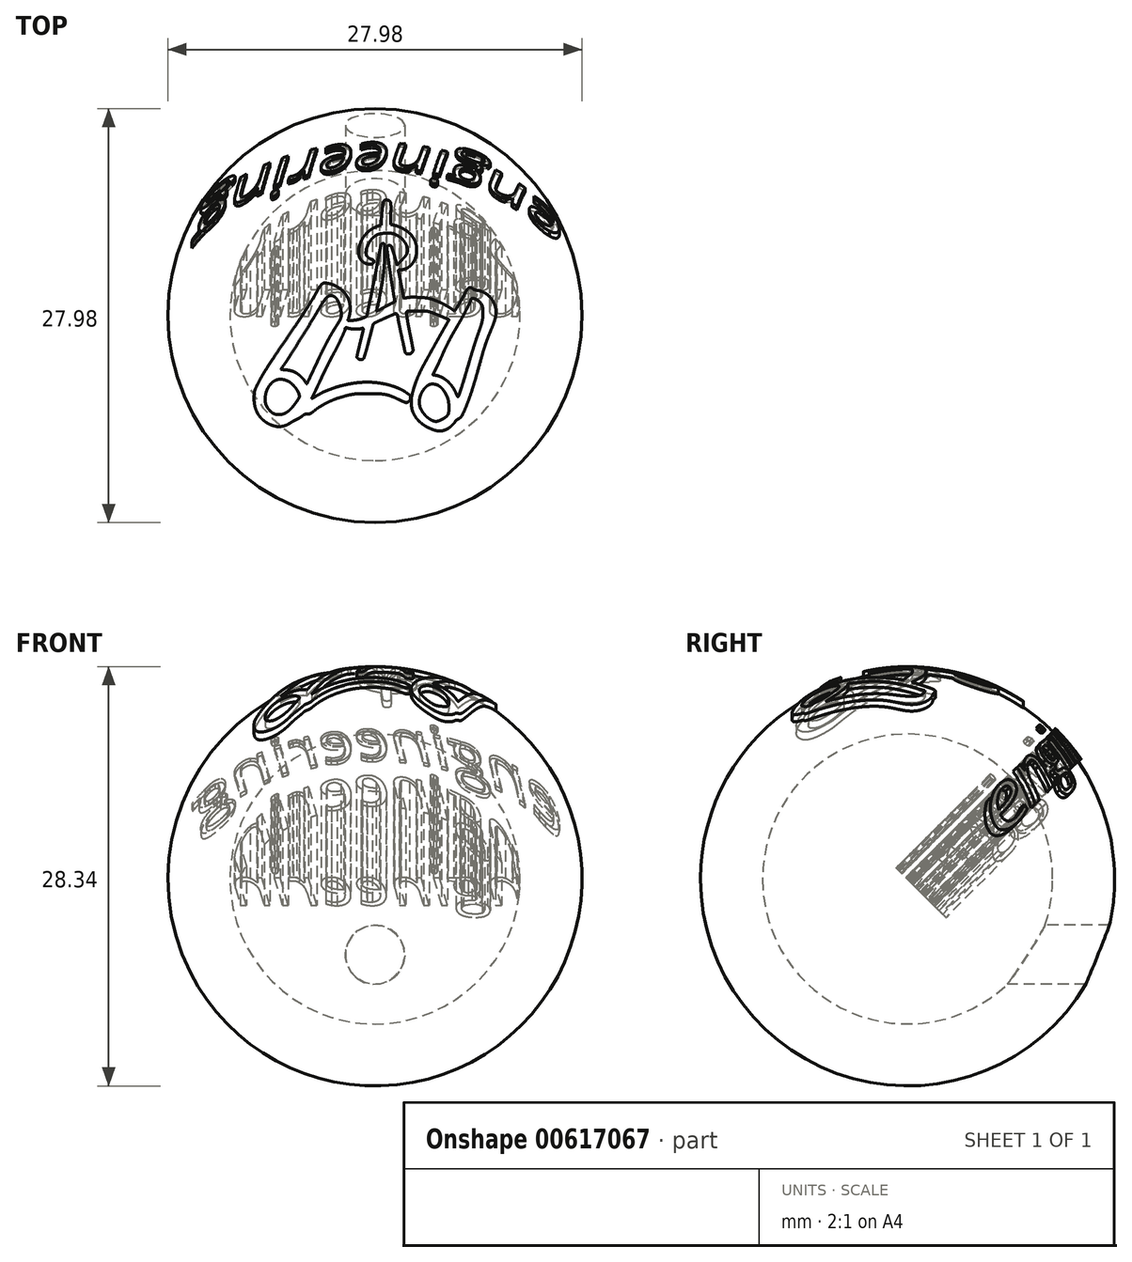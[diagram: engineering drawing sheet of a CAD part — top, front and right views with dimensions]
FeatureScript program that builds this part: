
annotation { "Feature Type Name" : "Feature", "Feature Type Description" : "" }
export const myFeature = defineFeature(function(context is Context, id is Id, definition is map)
    precondition{}
    {
        {
            var Q0;
            Q0=qCreatedBy(makeId("Top.planeOp"),FACE);
            var sketch = newSketch(context, id + "F0", { "sketchPlane" : qUnion([Q0])});
            skLineSegment(sketch, "E0", {"start": v(0, -10) * mm, "end": v(0, 10) * mm});
            skArc(sketch, "E1", {"start": v(0, 10) * mm, "mid": v(-10, 0) * mm, "end": v(0, -10) * mm});
            skSolve(sketch);
        }
        {
            var Q0;
            {var subQ0=sQuery(id+"F0.wireOp",EDGE,"E1");Q0=makeQuery(id+"F0.imprint","IMPRINT",FACE,{"disambiguationData":[TD([[makeQuery(id+"F0.imprint","IMPRINT",EDGE,{"derivedFrom":subQ0}),1.0]])]});}
            var Q1;
            Q1=sQuery(id+"F0.wireOp",EDGE,"E0");
            revolve(context, id + "F1", {"entities" : qUnion([Q0]), "axis" : qUnion([Q1]), "revolveType" : RevolveType.FULL});
        }
        {
            var Q0;
            Q0=makeQuery(id+"F1.opRevolve","SWEPT_BODY",BODY,{"disambiguationData":[OSD([sQuery(id+"F0.wireOp",EDGE,"E0"),sQuery(id+"F0.wireOp",EDGE,"E1")])]});
            var Q1;
            Q1=sQuery(id+"F0.wireOp",VERTEX,"NPe4G0ez-t7S9-9isL-QO5v-uuJu600mHcIT.center");
            var Q2;
            Q2=sQuery(id+"F0.wireOp",VERTEX,"E1.center");
            transform(context, id + "F2", {"entities" : qUnion([Q0]), "transformType" : TransformType.SCALE_UNIFORMLY, "scale" : 33.3, "scalePoint" : qUnion([Q2]), "makeCopy" : false});
        }
        {
            var Q0;
            Q0=qCreatedBy(makeId("Top.planeOp"),FACE);
            var sketch = newSketch(context, id + "F3", { "sketchPlane" : qUnion([Q0])});
            skArc(sketch, "E2", {"start": v(14.34, 184.46) * mm, "mid": v(13.65, 183.38) * mm, "end": v(13.25, 182.16) * mm});
            skArc(sketch, "E3", {"start": v(13.25, 182.16) * mm, "mid": v(12.71, 179.17) * mm, "end": v(12.25, 176.16) * mm});
            skArc(sketch, "E4", {"start": v(12.25, 176.16) * mm, "mid": v(11.73, 172.13) * mm, "end": v(11.32, 168.08) * mm});
            skArc(sketch, "E5", {"start": v(11.32, 168.08) * mm, "mid": v(10.9, 162.81) * mm, "end": v(10.53, 157.54) * mm});
            skLineSegment(sketch, "E6", {"start": v(10.53, 157.54) * mm, "end": v(9.8, 145.67) * mm});
            skLineSegment(sketch, "E7", {"start": v(9.8, 145.67) * mm, "end": v(3.78, 143.5) * mm});
            skArc(sketch, "E8", {"start": v(3.78, 143.5) * mm, "mid": v(-1.65, 141.13) * mm, "end": v(-6.72, 138.07) * mm});
            skArc(sketch, "E9", {"start": v(-6.72, 138.07) * mm, "mid": v(-11.38, 134.36) * mm, "end": v(-15.52, 130.08) * mm});
            skArc(sketch, "E10", {"start": v(-15.52, 130.08) * mm, "mid": v(-19.1, 125.3) * mm, "end": v(-22.03, 120.08) * mm});
            skArc(sketch, "E11", {"start": v(-22.03, 120.08) * mm, "mid": v(-24.3, 114.52) * mm, "end": v(-25.83, 108.72) * mm});
            skArc(sketch, "E12", {"start": v(-25.83, 108.72) * mm, "mid": v(-26.4, 104.16) * mm, "end": v(-26.28, 99.57) * mm});
            skArc(sketch, "E13", {"start": v(-26.28, 99.57) * mm, "mid": v(-25.48, 95.49) * mm, "end": v(-23.89, 91.65) * mm});
            skArc(sketch, "E14", {"start": v(-23.89, 91.65) * mm, "mid": v(-21.73, 88.51) * mm, "end": v(-18.93, 85.93) * mm});
            skArc(sketch, "E15", {"start": v(-18.93, 85.93) * mm, "mid": v(-15.67, 84.07) * mm, "end": v(-12.07, 83) * mm});
            skArc(sketch, "E16", {"start": v(-12.07, 83) * mm, "mid": v(-9.95, 82.7) * mm, "end": v(-7.82, 82.55) * mm});
            skArc(sketch, "E17", {"start": v(-7.82, 82.55) * mm, "mid": v(-6.26, 82.62) * mm, "end": v(-4.73, 82.96) * mm});
            skArc(sketch, "E18", {"start": v(-4.73, 82.96) * mm, "mid": v(-3.68, 83.44) * mm, "end": v(-2.8, 84.19) * mm});
            skArc(sketch, "E19", {"start": v(-2.8, 84.19) * mm, "mid": v(-2.19, 85.1) * mm, "end": v(-1.9, 86.15) * mm});
            skArc(sketch, "E20", {"start": v(-1.9, 86.15) * mm, "mid": v(-1.84, 86.88) * mm, "end": v(-1.86, 87.6) * mm});
            skArc(sketch, "E21", {"start": v(-1.86, 87.6) * mm, "mid": v(-1.96, 88.1) * mm, "end": v(-2.19, 88.56) * mm});
            skArc(sketch, "E22", {"start": v(-2.19, 88.56) * mm, "mid": v(-2.53, 88.96) * mm, "end": v(-2.96, 89.27) * mm});
            skArc(sketch, "E23", {"start": v(-2.96, 89.27) * mm, "mid": v(-3.66, 89.62) * mm, "end": v(-4.4, 89.92) * mm});
            skArc(sketch, "E24", {"start": v(-4.4, 89.92) * mm, "mid": v(-7.1, 91.04) * mm, "end": v(-9.71, 92.4) * mm});
            skArc(sketch, "E25", {"start": v(-9.71, 92.4) * mm, "mid": v(-11.45, 93.66) * mm, "end": v(-12.88, 95.27) * mm});
            skArc(sketch, "E26", {"start": v(-12.88, 95.27) * mm, "mid": v(-13.84, 97.04) * mm, "end": v(-14.34, 98.99) * mm});
            skArc(sketch, "E27", {"start": v(-14.34, 98.99) * mm, "mid": v(-14.52, 101.49) * mm, "end": v(-14.38, 104) * mm});
            skArc(sketch, "E28", {"start": v(-14.38, 104) * mm, "mid": v(-13.95, 106.46) * mm, "end": v(-13.24, 108.87) * mm});
            skArc(sketch, "E29", {"start": v(-13.24, 108.87) * mm, "mid": v(-12.08, 111.8) * mm, "end": v(-10.77, 114.65) * mm});
            skArc(sketch, "E30", {"start": v(-10.77, 114.65) * mm, "mid": v(-9.27, 117.46) * mm, "end": v(-7.61, 120.17) * mm});
            skArc(sketch, "E31", {"start": v(-7.61, 120.17) * mm, "mid": v(-6.07, 122.28) * mm, "end": v(-4.32, 124.22) * mm});
            skArc(sketch, "E32", {"start": v(-4.32, 124.22) * mm, "mid": v(-2.04, 126.3) * mm, "end": v(0.42, 128.16) * mm});
            skArc(sketch, "E33", {"start": v(0.42, 128.16) * mm, "mid": v(2.78, 129.56) * mm, "end": v(5.3, 130.64) * mm});
            skArc(sketch, "E34", {"start": v(5.3, 130.64) * mm, "mid": v(8.18, 131.48) * mm, "end": v(11.13, 131.98) * mm});
            skArc(sketch, "E35", {"start": v(11.13, 131.98) * mm, "mid": v(14.95, 132.3) * mm, "end": v(18.8, 132.4) * mm});
            skArc(sketch, "E36", {"start": v(18.8, 132.4) * mm, "mid": v(21.68, 132.38) * mm, "end": v(24.57, 132.3) * mm});
            skArc(sketch, "E37", {"start": v(24.57, 132.3) * mm, "mid": v(26.3, 132.18) * mm, "end": v(28.03, 131.95) * mm});
            skArc(sketch, "E38", {"start": v(28.03, 131.95) * mm, "mid": v(29.48, 131.62) * mm, "end": v(30.9, 131.17) * mm});
            skArc(sketch, "E39", {"start": v(30.9, 131.17) * mm, "mid": v(32.61, 130.47) * mm, "end": v(34.3, 129.7) * mm});
            skArc(sketch, "E40", {"start": v(34.3, 129.7) * mm, "mid": v(38, 127.6) * mm, "end": v(41.43, 125.08) * mm});
            skArc(sketch, "E41", {"start": v(41.43, 125.08) * mm, "mid": v(44.5, 122.2) * mm, "end": v(47.2, 118.99) * mm});
            skArc(sketch, "E42", {"start": v(47.2, 118.99) * mm, "mid": v(49.33, 115.7) * mm, "end": v(51, 112.16) * mm});
            skArc(sketch, "E43", {"start": v(51, 112.16) * mm, "mid": v(51.96, 108.85) * mm, "end": v(52.28, 105.42) * mm});
            skArc(sketch, "E44", {"start": v(52.28, 105.42) * mm, "mid": v(52.18, 103.4) * mm, "end": v(51.87, 101.4) * mm});
            skArc(sketch, "E45", {"start": v(51.87, 101.4) * mm, "mid": v(51.38, 99.73) * mm, "end": v(50.63, 98.17) * mm});
            skArc(sketch, "E46", {"start": v(50.63, 98.17) * mm, "mid": v(49.39, 96.27) * mm, "end": v(47.97, 94.5) * mm});
            skArc(sketch, "E47", {"start": v(47.97, 94.5) * mm, "mid": v(45.12, 91.31) * mm, "end": v(42.2, 88.18) * mm});
            skLineSegment(sketch, "E48", {"start": v(42.2, 88.18) * mm, "end": v(35.62, 81.22) * mm});
            skLineSegment(sketch, "E49", {"start": v(35.62, 81.22) * mm, "end": v(31.41, 95.8) * mm});
            skArc(sketch, "E50", {"start": v(31.41, 95.8) * mm, "mid": v(30.57, 98.66) * mm, "end": v(29.7, 101.5) * mm});
            skArc(sketch, "E51", {"start": v(29.7, 101.5) * mm, "mid": v(28.9, 104.02) * mm, "end": v(28.04, 106.52) * mm});
            skArc(sketch, "E52", {"start": v(28.04, 106.52) * mm, "mid": v(27.3, 108.6) * mm, "end": v(26.54, 110.68) * mm});
            skArc(sketch, "E53", {"start": v(26.54, 110.68) * mm, "mid": v(26.24, 111.27) * mm, "end": v(25.83, 111.78) * mm});
            skArc(sketch, "E54", {"start": v(25.83, 111.78) * mm, "mid": v(25.48, 112.08) * mm, "end": v(25.08, 112.32) * mm});
            skArc(sketch, "E55", {"start": v(25.08, 112.32) * mm, "mid": v(24.62, 112.5) * mm, "end": v(24.14, 112.63) * mm});
            skArc(sketch, "E56", {"start": v(24.14, 112.63) * mm, "mid": v(23.6, 112.7) * mm, "end": v(23.05, 112.7) * mm});
            skArc(sketch, "E57", {"start": v(23.05, 112.7) * mm, "mid": v(22.46, 112.63) * mm, "end": v(21.88, 112.51) * mm});
            skArc(sketch, "E58", {"start": v(21.88, 112.51) * mm, "mid": v(21.22, 112.3) * mm, "end": v(20.59, 112.04) * mm});
            skArc(sketch, "E59", {"start": v(20.59, 112.04) * mm, "mid": v(20.16, 111.77) * mm, "end": v(19.82, 111.4) * mm});
            skArc(sketch, "E60", {"start": v(19.82, 111.4) * mm, "mid": v(19.56, 110.94) * mm, "end": v(19.41, 110.43) * mm});
            skArc(sketch, "E61", {"start": v(19.41, 110.43) * mm, "mid": v(19.32, 109.68) * mm, "end": v(19.3, 108.93) * mm});
            skArc(sketch, "E62", {"start": v(19.3, 108.93) * mm, "mid": v(19.39, 106.06) * mm, "end": v(19.67, 103.2) * mm});
            skArc(sketch, "E63", {"start": v(19.67, 103.2) * mm, "mid": v(20.92, 93.82) * mm, "end": v(22.2, 84.45) * mm});
            skArc(sketch, "E64", {"start": v(22.2, 84.45) * mm, "mid": v(23.65, 74.23) * mm, "end": v(25.16, 64.02) * mm});
            skArc(sketch, "E65", {"start": v(25.16, 64.02) * mm, "mid": v(26.64, 54.39) * mm, "end": v(28.18, 44.76) * mm});
            skLineSegment(sketch, "E66", {"start": v(28.18, 44.76) * mm, "end": v(31.9, 22.13) * mm});
            skLineSegment(sketch, "E67", {"start": v(31.9, 22.13) * mm, "end": v(26.35, 19.42) * mm});
            skArc(sketch, "E68", {"start": v(26.35, 19.42) * mm, "mid": v(24.97, 18.74) * mm, "end": v(23.6, 18.04) * mm});
            skArc(sketch, "E69", {"start": v(23.6, 18.04) * mm, "mid": v(21.71, 17.05) * mm, "end": v(19.82, 16.05) * mm});
            skArc(sketch, "E70", {"start": v(19.82, 16.05) * mm, "mid": v(17.78, 14.95) * mm, "end": v(15.74, 13.84) * mm});
            skArc(sketch, "E71", {"start": v(15.74, 13.84) * mm, "mid": v(13.84, 12.8) * mm, "end": v(11.94, 11.74) * mm});
            skArc(sketch, "E72", {"start": v(11.94, 11.74) * mm, "mid": v(10.24, 10.8) * mm, "end": v(8.52, 9.86) * mm});
            skArc(sketch, "E73", {"start": v(8.52, 9.86) * mm, "mid": v(7.06, 9.08) * mm, "end": v(5.59, 8.33) * mm});
            skArc(sketch, "E74", {"start": v(5.59, 8.33) * mm, "mid": v(4.32, 7.7) * mm, "end": v(3.04, 7.07) * mm});
            skArc(sketch, "E75", {"start": v(3.04, 7.07) * mm, "mid": v(2.88, 7.04) * mm, "end": v(2.74, 7.12) * mm});
            skArc(sketch, "E76", {"start": v(2.74, 7.12) * mm, "mid": v(2.65, 7.27) * mm, "end": v(2.64, 7.44) * mm});
            skArc(sketch, "E77", {"start": v(2.64, 7.44) * mm, "mid": v(2.93, 9.01) * mm, "end": v(3.22, 10.58) * mm});
            skArc(sketch, "E78", {"start": v(3.22, 10.58) * mm, "mid": v(3.57, 12.38) * mm, "end": v(3.94, 14.18) * mm});
            skArc(sketch, "E79", {"start": v(3.94, 14.18) * mm, "mid": v(4.4, 16.3) * mm, "end": v(4.86, 18.4) * mm});
            skArc(sketch, "E80", {"start": v(4.86, 18.4) * mm, "mid": v(7.3, 29.7) * mm, "end": v(9.54, 41.06) * mm});
            skArc(sketch, "E81", {"start": v(9.54, 41.06) * mm, "mid": v(11.33, 51.39) * mm, "end": v(12.86, 61.75) * mm});
            skArc(sketch, "E82", {"start": v(12.86, 61.75) * mm, "mid": v(14.01, 71.25) * mm, "end": v(14.9, 80.77) * mm});
            skArc(sketch, "E83", {"start": v(14.9, 80.77) * mm, "mid": v(15.43, 89.58) * mm, "end": v(15.66, 98.4) * mm});
            skArc(sketch, "E84", {"start": v(15.66, 98.4) * mm, "mid": v(15.69, 103.78) * mm, "end": v(15.7, 109.17) * mm});
            skArc(sketch, "E85", {"start": v(15.7, 109.17) * mm, "mid": v(15.65, 111.11) * mm, "end": v(15.5, 113.05) * mm});
            skArc(sketch, "E86", {"start": v(15.5, 113.05) * mm, "mid": v(15.3, 114) * mm, "end": v(14.92, 114.88) * mm});
            skArc(sketch, "E87", {"start": v(14.92, 114.88) * mm, "mid": v(14.45, 115.4) * mm, "end": v(13.8, 115.66) * mm});
            skArc(sketch, "E88", {"start": v(13.8, 115.66) * mm, "mid": v(13.36, 115.7) * mm, "end": v(12.93, 115.7) * mm});
            skArc(sketch, "E89", {"start": v(12.93, 115.7) * mm, "mid": v(12.47, 115.66) * mm, "end": v(12.01, 115.6) * mm});
            skArc(sketch, "E90", {"start": v(12.01, 115.6) * mm, "mid": v(11.59, 115.51) * mm, "end": v(11.17, 115.4) * mm});
            skArc(sketch, "E91", {"start": v(11.17, 115.4) * mm, "mid": v(10.85, 115.27) * mm, "end": v(10.55, 115.1) * mm});
            skArc(sketch, "E92", {"start": v(10.55, 115.1) * mm, "mid": v(10.18, 114.74) * mm, "end": v(9.96, 114.27) * mm});
            skArc(sketch, "E93", {"start": v(9.96, 114.27) * mm, "mid": v(9.3, 111.54) * mm, "end": v(8.66, 108.8) * mm});
            skArc(sketch, "E94", {"start": v(8.66, 108.8) * mm, "mid": v(7.93, 105.55) * mm, "end": v(7.26, 102.3) * mm});
            skArc(sketch, "E95", {"start": v(7.26, 102.3) * mm, "mid": v(6.52, 98.49) * mm, "end": v(5.83, 94.68) * mm});
            skArc(sketch, "E96", {"start": v(5.83, 94.68) * mm, "mid": v(3.24, 80.45) * mm, "end": v(0.53, 66.24) * mm});
            skArc(sketch, "E97", {"start": v(0.53, 66.24) * mm, "mid": v(-2.7, 49.95) * mm, "end": v(-6.01, 33.68) * mm});
            skArc(sketch, "E98", {"start": v(-6.01, 33.68) * mm, "mid": v(-9.46, 17.03) * mm, "end": v(-12.92, 0.37) * mm});
            skArc(sketch, "E99", {"start": v(-12.92, 0.37) * mm, "mid": v(-13.36, -0.82) * mm, "end": v(-14.12, -1.85) * mm});
            skArc(sketch, "E100", {"start": v(-14.12, -1.85) * mm, "mid": v(-14.3, -2) * mm, "end": v(-14.5, -2.1) * mm});
            skArc(sketch, "E101", {"start": v(-14.5, -2.1) * mm, "mid": v(-15.47, -2.5) * mm, "end": v(-16.44, -2.9) * mm});
            skArc(sketch, "E102", {"start": v(-16.44, -2.9) * mm, "mid": v(-17.6, -3.36) * mm, "end": v(-18.75, -3.8) * mm});
            skArc(sketch, "E103", {"start": v(-18.75, -3.8) * mm, "mid": v(-20.07, -4.3) * mm, "end": v(-21.4, -4.8) * mm});
            skArc(sketch, "E104", {"start": v(-21.4, -4.8) * mm, "mid": v(-24.7, -5.86) * mm, "end": v(-28.07, -6.69) * mm});
            skArc(sketch, "E105", {"start": v(-28.07, -6.69) * mm, "mid": v(-31.93, -7.38) * mm, "end": v(-35.82, -7.87) * mm});
            skArc(sketch, "E106", {"start": v(-35.82, -7.87) * mm, "mid": v(-39.17, -8.14) * mm, "end": v(-42.54, -8.26) * mm});
            skArc(sketch, "E107", {"start": v(-42.54, -8.26) * mm, "mid": v(-43.31, -7.86) * mm, "end": v(-43.4, -7) * mm});
            skArc(sketch, "E108", {"start": v(-43.4, -7) * mm, "mid": v(-41.81, -2.55) * mm, "end": v(-40.64, 2.04) * mm});
            skArc(sketch, "E109", {"start": v(-40.64, 2.04) * mm, "mid": v(-39.95, 6.54) * mm, "end": v(-39.73, 11.1) * mm});
            skArc(sketch, "E110", {"start": v(-39.73, 11.1) * mm, "mid": v(-39.97, 15.5) * mm, "end": v(-40.7, 19.84) * mm});
            skArc(sketch, "E111", {"start": v(-40.7, 19.84) * mm, "mid": v(-41.86, 23.99) * mm, "end": v(-43.5, 27.97) * mm});
            skArc(sketch, "E112", {"start": v(-43.5, 27.97) * mm, "mid": v(-45.84, 32.18) * mm, "end": v(-48.67, 36.07) * mm});
            skArc(sketch, "E113", {"start": v(-48.67, 36.07) * mm, "mid": v(-52.02, 39.68) * mm, "end": v(-55.77, 42.88) * mm});
            skArc(sketch, "E114", {"start": v(-55.77, 42.88) * mm, "mid": v(-59.97, 45.73) * mm, "end": v(-64.46, 48.1) * mm});
            skArc(sketch, "E115", {"start": v(-64.46, 48.1) * mm, "mid": v(-69.32, 50.03) * mm, "end": v(-74.35, 51.47) * mm});
            skArc(sketch, "E116", {"start": v(-74.35, 51.47) * mm, "mid": v(-77.6, 52.06) * mm, "end": v(-80.88, 52.34) * mm});
            skArc(sketch, "E117", {"start": v(-80.88, 52.34) * mm, "mid": v(-82.95, 52.05) * mm, "end": v(-84.8, 51.08) * mm});
            skArc(sketch, "E118", {"start": v(-84.8, 51.08) * mm, "mid": v(-86.77, 49.23) * mm, "end": v(-88.38, 47.06) * mm});
            skArc(sketch, "E119", {"start": v(-88.38, 47.06) * mm, "mid": v(-91.9, 41.16) * mm, "end": v(-95.34, 35.2) * mm});
            skArc(sketch, "E120", {"start": v(-95.34, 35.2) * mm, "mid": v(-99.5, 28.01) * mm, "end": v(-103.77, 20.9) * mm});
            skArc(sketch, "E121", {"start": v(-103.77, 20.9) * mm, "mid": v(-108.75, 12.9) * mm, "end": v(-113.83, 4.98) * mm});
            skArc(sketch, "E122", {"start": v(-113.83, 4.98) * mm, "mid": v(-120.33, -4.92) * mm, "end": v(-126.92, -14.75) * mm});
            skArc(sketch, "E123", {"start": v(-126.92, -14.75) * mm, "mid": v(-135.97, -28.08) * mm, "end": v(-145.08, -41.37) * mm});
            skArc(sketch, "E124", {"start": v(-145.08, -41.37) * mm, "mid": v(-153.2, -53.26) * mm, "end": v(-161.26, -65.2) * mm});
            skArc(sketch, "E125", {"start": v(-161.26, -65.2) * mm, "mid": v(-167.24, -74.22) * mm, "end": v(-173.1, -83.34) * mm});
            skArc(sketch, "E126", {"start": v(-173.1, -83.34) * mm, "mid": v(-177.56, -90.54) * mm, "end": v(-181.9, -97.82) * mm});
            skArc(sketch, "E127", {"start": v(-181.9, -97.82) * mm, "mid": v(-185.29, -103.81) * mm, "end": v(-188.47, -109.91) * mm});
            skArc(sketch, "E128", {"start": v(-188.47, -109.91) * mm, "mid": v(-190.25, -113.53) * mm, "end": v(-192, -117.16) * mm});
            skArc(sketch, "E129", {"start": v(-192, -117.16) * mm, "mid": v(-192.8, -119.06) * mm, "end": v(-193.44, -121.02) * mm});
            skArc(sketch, "E130", {"start": v(-193.44, -121.02) * mm, "mid": v(-193.88, -122.88) * mm, "end": v(-194.14, -124.77) * mm});
            skArc(sketch, "E131", {"start": v(-194.14, -124.77) * mm, "mid": v(-194.37, -127.9) * mm, "end": v(-194.54, -131.03) * mm});
            skArc(sketch, "E132", {"start": v(-194.54, -131.03) * mm, "mid": v(-194.38, -138.24) * mm, "end": v(-193.34, -145.39) * mm});
            skArc(sketch, "E133", {"start": v(-193.34, -145.39) * mm, "mid": v(-191.48, -151.78) * mm, "end": v(-188.63, -157.8) * mm});
            skArc(sketch, "E134", {"start": v(-188.63, -157.8) * mm, "mid": v(-184.97, -163.14) * mm, "end": v(-180.5, -167.83) * mm});
            skArc(sketch, "E135", {"start": v(-180.5, -167.83) * mm, "mid": v(-175.16, -171.93) * mm, "end": v(-169.28, -175.21) * mm});
            skArc(sketch, "E136", {"start": v(-169.28, -175.21) * mm, "mid": v(-165, -176.93) * mm, "end": v(-160.56, -178.16) * mm});
            skArc(sketch, "E137", {"start": v(-160.56, -178.16) * mm, "mid": v(-156.38, -178.75) * mm, "end": v(-152.16, -178.74) * mm});
            skArc(sketch, "E138", {"start": v(-152.16, -178.74) * mm, "mid": v(-147.99, -178.12) * mm, "end": v(-143.95, -176.9) * mm});
            skArc(sketch, "E139", {"start": v(-143.95, -176.9) * mm, "mid": v(-139.78, -175.02) * mm, "end": v(-135.84, -172.69) * mm});
            skArc(sketch, "E140", {"start": v(-135.84, -172.69) * mm, "mid": v(-134.67, -171.92) * mm, "end": v(-133.48, -171.19) * mm});
            skArc(sketch, "E141", {"start": v(-133.48, -171.19) * mm, "mid": v(-132.02, -170.33) * mm, "end": v(-130.56, -169.5) * mm});
            skArc(sketch, "E142", {"start": v(-130.56, -169.5) * mm, "mid": v(-129.07, -168.68) * mm, "end": v(-127.57, -167.89) * mm});
            skArc(sketch, "E143", {"start": v(-127.57, -167.89) * mm, "mid": v(-126.28, -167.24) * mm, "end": v(-124.99, -166.63) * mm});
            skArc(sketch, "E144", {"start": v(-124.99, -166.63) * mm, "mid": v(-123.77, -166.04) * mm, "end": v(-122.57, -165.42) * mm});
            skArc(sketch, "E145", {"start": v(-122.57, -165.42) * mm, "mid": v(-121.31, -164.71) * mm, "end": v(-120.08, -163.97) * mm});
            skArc(sketch, "E146", {"start": v(-120.08, -163.97) * mm, "mid": v(-118.96, -163.26) * mm, "end": v(-117.87, -162.51) * mm});
            skArc(sketch, "E147", {"start": v(-117.87, -162.51) * mm, "mid": v(-117.11, -161.93) * mm, "end": v(-116.4, -161.3) * mm});
            skArc(sketch, "E148", {"start": v(-116.4, -161.3) * mm, "mid": v(-115.6, -160.59) * mm, "end": v(-114.75, -159.94) * mm});
            skArc(sketch, "E149", {"start": v(-114.75, -159.94) * mm, "mid": v(-114, -159.49) * mm, "end": v(-113.2, -159.14) * mm});
            skArc(sketch, "E150", {"start": v(-113.2, -159.14) * mm, "mid": v(-112.29, -158.88) * mm, "end": v(-111.36, -158.73) * mm});
            skArc(sketch, "E151", {"start": v(-111.36, -158.73) * mm, "mid": v(-110.1, -158.63) * mm, "end": v(-108.83, -158.6) * mm});
            skArc(sketch, "E152", {"start": v(-108.83, -158.6) * mm, "mid": v(-107.46, -158.56) * mm, "end": v(-106.1, -158.42) * mm});
            skArc(sketch, "E153", {"start": v(-106.1, -158.42) * mm, "mid": v(-105.05, -158.22) * mm, "end": v(-104.05, -157.87) * mm});
            skArc(sketch, "E154", {"start": v(-104.05, -157.87) * mm, "mid": v(-103, -157.36) * mm, "end": v(-102, -156.73) * mm});
            skArc(sketch, "E155", {"start": v(-102, -156.73) * mm, "mid": v(-100.56, -155.65) * mm, "end": v(-99.15, -154.52) * mm});
            skArc(sketch, "E156", {"start": v(-99.15, -154.52) * mm, "mid": v(-93.2, -149.94) * mm, "end": v(-86.94, -145.77) * mm});
            skArc(sketch, "E157", {"start": v(-86.94, -145.77) * mm, "mid": v(-80.24, -141.9) * mm, "end": v(-73.3, -138.46) * mm});
            skArc(sketch, "E158", {"start": v(-73.3, -138.46) * mm, "mid": v(-65.76, -135.26) * mm, "end": v(-58.04, -132.51) * mm});
            skArc(sketch, "E159", {"start": v(-58.04, -132.51) * mm, "mid": v(-49.56, -129.99) * mm, "end": v(-40.97, -127.85) * mm});
            skArc(sketch, "E160", {"start": v(-40.97, -127.85) * mm, "mid": v(-37.92, -127.23) * mm, "end": v(-34.86, -126.7) * mm});
            skArc(sketch, "E161", {"start": v(-34.86, -126.7) * mm, "mid": v(-32, -126.32) * mm, "end": v(-29.13, -126.06) * mm});
            skArc(sketch, "E162", {"start": v(-29.13, -126.06) * mm, "mid": v(-25.47, -125.86) * mm, "end": v(-21.81, -125.76) * mm});
            skArc(sketch, "E163", {"start": v(-21.81, -125.76) * mm, "mid": v(-15.76, -125.7) * mm, "end": v(-9.7, -125.7) * mm});
            skArc(sketch, "E164", {"start": v(-9.7, -125.7) * mm, "mid": v(-1.4, -125.79) * mm, "end": v(6.9, -126.06) * mm});
            skArc(sketch, "E165", {"start": v(6.9, -126.06) * mm, "mid": v(12.17, -126.49) * mm, "end": v(17.4, -127.32) * mm});
            skArc(sketch, "E166", {"start": v(17.4, -127.32) * mm, "mid": v(22.02, -128.45) * mm, "end": v(26.52, -130) * mm});
            skArc(sketch, "E167", {"start": v(26.52, -130) * mm, "mid": v(32.23, -132.42) * mm, "end": v(37.83, -135.08) * mm});
            skArc(sketch, "E168", {"start": v(37.83, -135.08) * mm, "mid": v(39.82, -136.05) * mm, "end": v(41.82, -137) * mm});
            skArc(sketch, "E169", {"start": v(41.82, -137) * mm, "mid": v(43.67, -137.83) * mm, "end": v(45.53, -138.62) * mm});
            skArc(sketch, "E170", {"start": v(45.53, -138.62) * mm, "mid": v(47.09, -139.26) * mm, "end": v(48.65, -139.86) * mm});
            skArc(sketch, "E171", {"start": v(48.65, -139.86) * mm, "mid": v(49.29, -140.04) * mm, "end": v(49.94, -140.1) * mm});
            skArc(sketch, "E172", {"start": v(49.94, -140.1) * mm, "mid": v(51.3, -139.95) * mm, "end": v(52.6, -139.5) * mm});
            skArc(sketch, "E173", {"start": v(52.6, -139.5) * mm, "mid": v(53.87, -138.72) * mm, "end": v(55, -137.74) * mm});
            skArc(sketch, "E174", {"start": v(55, -137.74) * mm, "mid": v(55.96, -136.58) * mm, "end": v(56.7, -135.26) * mm});
            skArc(sketch, "E175", {"start": v(56.7, -135.26) * mm, "mid": v(57.14, -133.93) * mm, "end": v(57.3, -132.54) * mm});
            skArc(sketch, "E176", {"start": v(57.3, -132.54) * mm, "mid": v(57.24, -131.55) * mm, "end": v(57.08, -130.58) * mm});
            skArc(sketch, "E177", {"start": v(57.08, -130.58) * mm, "mid": v(56.83, -129.8) * mm, "end": v(56.44, -129.1) * mm});
            skArc(sketch, "E178", {"start": v(56.44, -129.1) * mm, "mid": v(55.82, -128.32) * mm, "end": v(55.11, -127.63) * mm});
            skArc(sketch, "E179", {"start": v(55.11, -127.63) * mm, "mid": v(53.84, -126.59) * mm, "end": v(52.54, -125.59) * mm});
            skArc(sketch, "E180", {"start": v(52.54, -125.59) * mm, "mid": v(47.48, -122.16) * mm, "end": v(42.12, -119.2) * mm});
            skArc(sketch, "E181", {"start": v(42.12, -119.2) * mm, "mid": v(35.97, -116.42) * mm, "end": v(29.64, -114.04) * mm});
            skArc(sketch, "E182", {"start": v(29.64, -114.04) * mm, "mid": v(22.62, -111.91) * mm, "end": v(15.48, -110.22) * mm});
            skArc(sketch, "E183", {"start": v(15.48, -110.22) * mm, "mid": v(7.8, -108.85) * mm, "end": v(0.07, -107.87) * mm});
            skArc(sketch, "E184", {"start": v(0.07, -107.87) * mm, "mid": v(-11.56, -107.24) * mm, "end": v(-23.2, -107.67) * mm});
            skArc(sketch, "E185", {"start": v(-23.2, -107.67) * mm, "mid": v(-35.8, -109.16) * mm, "end": v(-48.27, -111.52) * mm});
            skArc(sketch, "E186", {"start": v(-48.27, -111.52) * mm, "mid": v(-60.58, -114.77) * mm, "end": v(-72.63, -118.87) * mm});
            skArc(sketch, "E187", {"start": v(-72.63, -118.87) * mm, "mid": v(-83.4, -123.52) * mm, "end": v(-93.73, -129.11) * mm});
            skArc(sketch, "E188", {"start": v(-93.73, -129.11) * mm, "mid": v(-95.26, -130.02) * mm, "end": v(-96.8, -130.92) * mm});
            skArc(sketch, "E189", {"start": v(-96.8, -130.92) * mm, "mid": v(-98.07, -131.66) * mm, "end": v(-99.37, -132.37) * mm});
            skArc(sketch, "E190", {"start": v(-99.37, -132.37) * mm, "mid": v(-100.46, -132.97) * mm, "end": v(-101.56, -133.57) * mm});
            skArc(sketch, "E191", {"start": v(-101.56, -133.57) * mm, "mid": v(-101.66, -133.57) * mm, "end": v(-101.7, -133.48) * mm});
            skArc(sketch, "E192", {"start": v(-101.7, -133.48) * mm, "mid": v(-101.7, -133.32) * mm, "end": v(-101.64, -133.17) * mm});
            skArc(sketch, "E193", {"start": v(-101.64, -133.17) * mm, "mid": v(-101.08, -131.99) * mm, "end": v(-100.52, -130.8) * mm});
            skArc(sketch, "E194", {"start": v(-100.52, -130.8) * mm, "mid": v(-99.86, -129.45) * mm, "end": v(-99.2, -128.1) * mm});
            skArc(sketch, "E195", {"start": v(-99.2, -128.1) * mm, "mid": v(-98.43, -126.54) * mm, "end": v(-97.65, -124.98) * mm});
            skArc(sketch, "E196", {"start": v(-97.65, -124.98) * mm, "mid": v(-96.6, -122.86) * mm, "end": v(-95.56, -120.72) * mm});
            skArc(sketch, "E197", {"start": v(-95.56, -120.72) * mm, "mid": v(-94, -117.43) * mm, "end": v(-92.45, -114.14) * mm});
            skArc(sketch, "E198", {"start": v(-92.45, -114.14) * mm, "mid": v(-90.72, -110.43) * mm, "end": v(-89, -106.7) * mm});
            skArc(sketch, "E199", {"start": v(-89, -106.7) * mm, "mid": v(-87.32, -103.07) * mm, "end": v(-85.66, -99.43) * mm});
            skArc(sketch, "E200", {"start": v(-85.66, -99.43) * mm, "mid": v(-83.79, -95.37) * mm, "end": v(-81.86, -91.34) * mm});
            skArc(sketch, "E201", {"start": v(-81.86, -91.34) * mm, "mid": v(-79.41, -86.34) * mm, "end": v(-76.93, -81.36) * mm});
            skArc(sketch, "E202", {"start": v(-76.93, -81.36) * mm, "mid": v(-74.35, -76.27) * mm, "end": v(-71.74, -71.2) * mm});
            skArc(sketch, "E203", {"start": v(-71.74, -71.2) * mm, "mid": v(-69.44, -66.8) * mm, "end": v(-67.1, -62.45) * mm});
            skArc(sketch, "E204", {"start": v(-67.1, -62.45) * mm, "mid": v(-63.55, -55.84) * mm, "end": v(-60.13, -49.17) * mm});
            skArc(sketch, "E205", {"start": v(-60.13, -49.17) * mm, "mid": v(-56.9, -42.6) * mm, "end": v(-53.78, -35.96) * mm});
            skArc(sketch, "E206", {"start": v(-53.78, -35.96) * mm, "mid": v(-51.14, -30.12) * mm, "end": v(-48.56, -24.25) * mm});
            skArc(sketch, "E207", {"start": v(-48.56, -24.25) * mm, "mid": v(-47.94, -22.29) * mm, "end": v(-47.72, -20.24) * mm});
            skArc(sketch, "E208", {"start": v(-47.72, -20.24) * mm, "mid": v(-47.69, -19.98) * mm, "end": v(-47.6, -19.73) * mm});
            skArc(sketch, "E209", {"start": v(-47.6, -19.73) * mm, "mid": v(-47.46, -19.54) * mm, "end": v(-47.28, -19.42) * mm});
            skArc(sketch, "E210", {"start": v(-47.28, -19.42) * mm, "mid": v(-47.02, -19.34) * mm, "end": v(-46.76, -19.34) * mm});
            skArc(sketch, "E211", {"start": v(-46.76, -19.34) * mm, "mid": v(-46.41, -19.4) * mm, "end": v(-46.08, -19.51) * mm});
            skArc(sketch, "E212", {"start": v(-46.08, -19.51) * mm, "mid": v(-43.19, -20.46) * mm, "end": v(-40.21, -21.12) * mm});
            skArc(sketch, "E213", {"start": v(-40.21, -21.12) * mm, "mid": v(-36.72, -21.6) * mm, "end": v(-33.21, -21.85) * mm});
            skArc(sketch, "E214", {"start": v(-33.21, -21.85) * mm, "mid": v(-29.67, -21.87) * mm, "end": v(-26.14, -21.67) * mm});
            skArc(sketch, "E215", {"start": v(-26.14, -21.67) * mm, "mid": v(-23.07, -21.25) * mm, "end": v(-20.05, -20.53) * mm});
            skArc(sketch, "E216", {"start": v(-20.05, -20.53) * mm, "mid": v(-19.45, -20.61) * mm, "end": v(-19.08, -21.1) * mm});
            skArc(sketch, "E217", {"start": v(-19.08, -21.1) * mm, "mid": v(-18.94, -22.16) * mm, "end": v(-19, -23.23) * mm});
            skArc(sketch, "E218", {"start": v(-19, -23.23) * mm, "mid": v(-19.47, -25.76) * mm, "end": v(-20.03, -28.26) * mm});
            skArc(sketch, "E219", {"start": v(-20.03, -28.26) * mm, "mid": v(-21.82, -35.52) * mm, "end": v(-23.63, -42.78) * mm});
            skArc(sketch, "E220", {"start": v(-23.63, -42.78) * mm, "mid": v(-24.72, -47.21) * mm, "end": v(-25.8, -51.65) * mm});
            skArc(sketch, "E221", {"start": v(-25.8, -51.65) * mm, "mid": v(-26.69, -55.5) * mm, "end": v(-27.55, -59.36) * mm});
            skArc(sketch, "E222", {"start": v(-27.55, -59.36) * mm, "mid": v(-28.26, -62.68) * mm, "end": v(-28.97, -66) * mm});
            skArc(sketch, "E223", {"start": v(-28.97, -66) * mm, "mid": v(-29.01, -66.56) * mm, "end": v(-28.92, -67.12) * mm});
            skArc(sketch, "E224", {"start": v(-28.92, -67.12) * mm, "mid": v(-28.28, -68.45) * mm, "end": v(-27.27, -69.52) * mm});
            skArc(sketch, "E225", {"start": v(-27.27, -69.52) * mm, "mid": v(-25.86, -70.38) * mm, "end": v(-24.29, -70.9) * mm});
            skArc(sketch, "E226", {"start": v(-24.29, -70.9) * mm, "mid": v(-22.64, -71.06) * mm, "end": v(-21, -70.86) * mm});
            skArc(sketch, "E227", {"start": v(-21, -70.86) * mm, "mid": v(-19.62, -70.3) * mm, "end": v(-18.48, -69.35) * mm});
            skArc(sketch, "E228", {"start": v(-18.48, -69.35) * mm, "mid": v(-18, -68.67) * mm, "end": v(-17.66, -67.9) * mm});
            skArc(sketch, "E229", {"start": v(-17.66, -67.9) * mm, "mid": v(-16.54, -64.27) * mm, "end": v(-15.43, -60.62) * mm});
            skArc(sketch, "E230", {"start": v(-15.43, -60.62) * mm, "mid": v(-14.16, -56.32) * mm, "end": v(-12.94, -52) * mm});
            skArc(sketch, "E231", {"start": v(-12.94, -52) * mm, "mid": v(-11.59, -47.05) * mm, "end": v(-10.28, -42.1) * mm});
            skArc(sketch, "E232", {"start": v(-10.28, -42.1) * mm, "mid": v(-8.98, -37.15) * mm, "end": v(-7.68, -32.2) * mm});
            skArc(sketch, "E233", {"start": v(-7.68, -32.2) * mm, "mid": v(-6.55, -27.87) * mm, "end": v(-5.41, -23.54) * mm});
            skArc(sketch, "E234", {"start": v(-5.41, -23.54) * mm, "mid": v(-4.43, -19.83) * mm, "end": v(-3.45, -16.13) * mm});
            skArc(sketch, "E235", {"start": v(-3.45, -16.13) * mm, "mid": v(-3.26, -15.43) * mm, "end": v(-3.06, -14.74) * mm});
            skArc(sketch, "E236", {"start": v(-3.06, -14.74) * mm, "mid": v(-2.13, -13.04) * mm, "end": v(-0.59, -11.86) * mm});
            skArc(sketch, "E237", {"start": v(-0.59, -11.86) * mm, "mid": v(7.47, -8.13) * mm, "end": v(15.57, -4.48) * mm});
            skArc(sketch, "E238", {"start": v(15.57, -4.48) * mm, "mid": v(23.74, -0.89) * mm, "end": v(31.95, 2.62) * mm});
            skArc(sketch, "E239", {"start": v(31.95, 2.62) * mm, "mid": v(33.7, 2.9) * mm, "end": v(35.37, 2.35) * mm});
            skArc(sketch, "E240", {"start": v(35.37, 2.35) * mm, "mid": v(35.56, 2.18) * mm, "end": v(35.67, 1.96) * mm});
            skArc(sketch, "E241", {"start": v(35.67, 1.96) * mm, "mid": v(35.88, 1.31) * mm, "end": v(36.06, 0.65) * mm});
            skArc(sketch, "E242", {"start": v(36.06, 0.65) * mm, "mid": v(36.26, -0.16) * mm, "end": v(36.44, -0.98) * mm});
            skArc(sketch, "E243", {"start": v(36.44, -0.98) * mm, "mid": v(36.6, -1.9) * mm, "end": v(36.75, -2.84) * mm});
            skArc(sketch, "E244", {"start": v(36.75, -2.84) * mm, "mid": v(37.64, -8.37) * mm, "end": v(38.7, -13.88) * mm});
            skArc(sketch, "E245", {"start": v(38.7, -13.88) * mm, "mid": v(40.96, -24.57) * mm, "end": v(43.27, -35.24) * mm});
            skArc(sketch, "E246", {"start": v(43.27, -35.24) * mm, "mid": v(45.85, -47) * mm, "end": v(48.44, -58.74) * mm});
            skArc(sketch, "E247", {"start": v(48.44, -58.74) * mm, "mid": v(48.81, -59.8) * mm, "end": v(49.43, -60.76) * mm});
            skArc(sketch, "E248", {"start": v(49.43, -60.76) * mm, "mid": v(50.25, -61.48) * mm, "end": v(51.26, -61.9) * mm});
            skArc(sketch, "E249", {"start": v(51.26, -61.9) * mm, "mid": v(52.64, -62.1) * mm, "end": v(54.03, -62.07) * mm});
            skArc(sketch, "E250", {"start": v(54.03, -62.07) * mm, "mid": v(55.5, -61.8) * mm, "end": v(56.92, -61.32) * mm});
            skArc(sketch, "E251", {"start": v(56.92, -61.32) * mm, "mid": v(58.1, -60.67) * mm, "end": v(59.12, -59.79) * mm});
            skArc(sketch, "E252", {"start": v(59.12, -59.79) * mm, "mid": v(59.55, -59.3) * mm, "end": v(59.95, -58.77) * mm});
            skArc(sketch, "E253", {"start": v(59.95, -58.77) * mm, "mid": v(60.32, -58.21) * mm, "end": v(60.65, -57.63) * mm});
            skArc(sketch, "E254", {"start": v(60.65, -57.63) * mm, "mid": v(60.92, -57.1) * mm, "end": v(61.14, -56.55) * mm});
            skArc(sketch, "E255", {"start": v(61.14, -56.55) * mm, "mid": v(61.25, -56.14) * mm, "end": v(61.3, -55.71) * mm});
            skArc(sketch, "E256", {"start": v(61.3, -55.71) * mm, "mid": v(61.26, -55.09) * mm, "end": v(61.18, -54.47) * mm});
            skArc(sketch, "E257", {"start": v(61.18, -54.47) * mm, "mid": v(60.74, -52.02) * mm, "end": v(60.3, -49.57) * mm});
            skArc(sketch, "E258", {"start": v(60.3, -49.57) * mm, "mid": v(59.75, -46.68) * mm, "end": v(59.19, -43.8) * mm});
            skArc(sketch, "E259", {"start": v(59.19, -43.8) * mm, "mid": v(58.54, -40.53) * mm, "end": v(57.88, -37.28) * mm});
            skArc(sketch, "E260", {"start": v(57.88, -37.28) * mm, "mid": v(55.91, -27.49) * mm, "end": v(54, -17.7) * mm});
            skArc(sketch, "E261", {"start": v(54, -17.7) * mm, "mid": v(52.83, -11.3) * mm, "end": v(51.78, -4.89) * mm});
            skArc(sketch, "E262", {"start": v(51.78, -4.89) * mm, "mid": v(51.12, -0.35) * mm, "end": v(50.51, 4.2) * mm});
            skArc(sketch, "E263", {"start": v(50.51, 4.2) * mm, "mid": v(50.63, 5.29) * mm, "end": v(51.2, 6.22) * mm});
            skArc(sketch, "E264", {"start": v(51.2, 6.21) * mm, "mid": v(51.73, 6.59) * mm, "end": v(52.35, 6.77) * mm});
            skArc(sketch, "E265", {"start": v(52.35, 6.77) * mm, "mid": v(54.2, 6.96) * mm, "end": v(56.05, 7.1) * mm});
            skArc(sketch, "E266", {"start": v(56.05, 7.1) * mm, "mid": v(58.64, 7.24) * mm, "end": v(61.23, 7.32) * mm});
            skArc(sketch, "E267", {"start": v(61.23, 7.32) * mm, "mid": v(64.9, 7.38) * mm, "end": v(68.58, 7.4) * mm});
            skArc(sketch, "E268", {"start": v(68.58, 7.4) * mm, "mid": v(74.4, 7.35) * mm, "end": v(80.22, 7.23) * mm});
            skArc(sketch, "E269", {"start": v(80.22, 7.23) * mm, "mid": v(83.05, 7) * mm, "end": v(85.84, 6.5) * mm});
            skArc(sketch, "E270", {"start": v(85.84, 6.5) * mm, "mid": v(88.83, 5.69) * mm, "end": v(91.74, 4.65) * mm});
            skArc(sketch, "E271", {"start": v(91.74, 4.65) * mm, "mid": v(99.27, 1.6) * mm, "end": v(106.8, -1.5) * mm});
            skArc(sketch, "E272", {"start": v(106.8, -1.5) * mm, "mid": v(108.93, -2.4) * mm, "end": v(111.06, -3.28) * mm});
            skArc(sketch, "E273", {"start": v(111.06, -3.28) * mm, "mid": v(112.93, -4.05) * mm, "end": v(114.8, -4.82) * mm});
            skArc(sketch, "E274", {"start": v(114.8, -4.82) * mm, "mid": v(116.4, -5.48) * mm, "end": v(118, -6.13) * mm});
            skArc(sketch, "E275", {"start": v(118, -6.13) * mm, "mid": v(118.29, -6.25) * mm, "end": v(118.58, -6.35) * mm});
            skArc(sketch, "E276", {"start": v(118.58, -6.35) * mm, "mid": v(118.74, -6.5) * mm, "end": v(118.74, -6.73) * mm});
            skArc(sketch, "E277", {"start": v(118.74, -6.73) * mm, "mid": v(118.08, -8.1) * mm, "end": v(117.41, -9.48) * mm});
            skArc(sketch, "E278", {"start": v(117.41, -9.48) * mm, "mid": v(116.57, -11.13) * mm, "end": v(115.69, -12.76) * mm});
            skArc(sketch, "E279", {"start": v(115.69, -12.76) * mm, "mid": v(114.6, -14.7) * mm, "end": v(113.49, -16.61) * mm});
            skArc(sketch, "E280", {"start": v(113.49, -16.61) * mm, "mid": v(112.03, -19.1) * mm, "end": v(110.59, -21.61) * mm});
            skArc(sketch, "E281", {"start": v(110.59, -21.61) * mm, "mid": v(108.58, -25.13) * mm, "end": v(106.58, -28.66) * mm});
            skArc(sketch, "E282", {"start": v(106.58, -28.66) * mm, "mid": v(104.42, -32.5) * mm, "end": v(102.26, -36.36) * mm});
            skArc(sketch, "E283", {"start": v(102.26, -36.36) * mm, "mid": v(100.24, -39.98) * mm, "end": v(98.24, -43.6) * mm});
            skArc(sketch, "E284", {"start": v(98.24, -43.6) * mm, "mid": v(96.16, -47.36) * mm, "end": v(94.08, -51.13) * mm});
            skArc(sketch, "E285", {"start": v(94.08, -51.13) * mm, "mid": v(91.7, -55.42) * mm, "end": v(89.33, -59.72) * mm});
            skArc(sketch, "E286", {"start": v(89.33, -59.72) * mm, "mid": v(87.03, -63.87) * mm, "end": v(84.73, -68.02) * mm});
            skArc(sketch, "E287", {"start": v(84.73, -68.02) * mm, "mid": v(82.9, -71.31) * mm, "end": v(81.08, -74.6) * mm});
            skArc(sketch, "E288", {"start": v(81.08, -74.6) * mm, "mid": v(77.18, -81.83) * mm, "end": v(73.45, -89.14) * mm});
            skArc(sketch, "E289", {"start": v(73.45, -89.14) * mm, "mid": v(70.46, -95.48) * mm, "end": v(67.73, -101.92) * mm});
            skArc(sketch, "E290", {"start": v(67.73, -101.92) * mm, "mid": v(65.34, -108.25) * mm, "end": v(63.2, -114.68) * mm});
            skArc(sketch, "E291", {"start": v(63.2, -114.68) * mm, "mid": v(61.1, -121.86) * mm, "end": v(59.2, -129.1) * mm});
            skArc(sketch, "E292", {"start": v(59.2, -129.1) * mm, "mid": v(58.72, -131.55) * mm, "end": v(58.46, -134.03) * mm});
            skArc(sketch, "E293", {"start": v(58.46, -134.03) * mm, "mid": v(58.35, -137.28) * mm, "end": v(58.38, -140.54) * mm});
            skArc(sketch, "E294", {"start": v(58.38, -140.54) * mm, "mid": v(58.54, -143.81) * mm, "end": v(58.85, -147.08) * mm});
            skArc(sketch, "E295", {"start": v(58.85, -147.08) * mm, "mid": v(59.26, -149.65) * mm, "end": v(59.88, -152.17) * mm});
            skArc(sketch, "E296", {"start": v(59.88, -152.17) * mm, "mid": v(61.41, -156.43) * mm, "end": v(63.45, -160.48) * mm});
            skArc(sketch, "E297", {"start": v(63.45, -160.48) * mm, "mid": v(66.06, -164.47) * mm, "end": v(69.06, -168.16) * mm});
            skArc(sketch, "E298", {"start": v(69.06, -168.16) * mm, "mid": v(72.6, -171.69) * mm, "end": v(76.47, -174.86) * mm});
            skArc(sketch, "E299", {"start": v(76.47, -174.86) * mm, "mid": v(80.8, -177.77) * mm, "end": v(85.36, -180.29) * mm});
            skArc(sketch, "E300", {"start": v(85.36, -180.29) * mm, "mid": v(89.87, -182.36) * mm, "end": v(94.49, -184.15) * mm});
            skArc(sketch, "E301", {"start": v(94.49, -184.15) * mm, "mid": v(98.19, -185.21) * mm, "end": v(102, -185.8) * mm});
            skArc(sketch, "E302", {"start": v(102, -185.8) * mm, "mid": v(105.4, -185.85) * mm, "end": v(108.76, -185.39) * mm});
            skArc(sketch, "E303", {"start": v(108.76, -185.39) * mm, "mid": v(112.23, -184.42) * mm, "end": v(115.54, -183.01) * mm});
            skArc(sketch, "E304", {"start": v(115.54, -183.01) * mm, "mid": v(117.5, -181.93) * mm, "end": v(119.35, -180.7) * mm});
            skArc(sketch, "E305", {"start": v(119.35, -180.7) * mm, "mid": v(121.38, -179.14) * mm, "end": v(123.32, -177.46) * mm});
            skArc(sketch, "E306", {"start": v(123.32, -177.46) * mm, "mid": v(125.09, -175.76) * mm, "end": v(126.76, -173.96) * mm});
            skArc(sketch, "E307", {"start": v(126.76, -173.96) * mm, "mid": v(127.92, -172.47) * mm, "end": v(128.9, -170.85) * mm});
            skArc(sketch, "E308", {"start": v(128.9, -170.85) * mm, "mid": v(129.26, -170.25) * mm, "end": v(129.68, -169.7) * mm});
            skArc(sketch, "E309", {"start": v(129.68, -169.7) * mm, "mid": v(130.25, -169.09) * mm, "end": v(130.86, -168.51) * mm});
            skArc(sketch, "E310", {"start": v(130.86, -168.51) * mm, "mid": v(131.53, -167.97) * mm, "end": v(132.22, -167.46) * mm});
            skArc(sketch, "E311", {"start": v(132.22, -167.46) * mm, "mid": v(132.88, -167.07) * mm, "end": v(133.57, -166.74) * mm});
            skArc(sketch, "E312", {"start": v(133.57, -166.74) * mm, "mid": v(135.12, -165.97) * mm, "end": v(136.56, -165) * mm});
            skArc(sketch, "E313", {"start": v(136.56, -165) * mm, "mid": v(137.77, -163.93) * mm, "end": v(138.8, -162.68) * mm});
            skArc(sketch, "E314", {"start": v(138.8, -162.68) * mm, "mid": v(140.01, -160.8) * mm, "end": v(141.06, -158.8) * mm});
            skArc(sketch, "E315", {"start": v(141.06, -158.8) * mm, "mid": v(142.85, -154.97) * mm, "end": v(144.58, -151.1) * mm});
            skArc(sketch, "E316", {"start": v(144.58, -151.1) * mm, "mid": v(147.12, -145.08) * mm, "end": v(149.48, -139) * mm});
            skArc(sketch, "E317", {"start": v(149.48, -139) * mm, "mid": v(152.14, -131.65) * mm, "end": v(154.67, -124.27) * mm});
            skArc(sketch, "E318", {"start": v(154.67, -124.27) * mm, "mid": v(157.4, -115.85) * mm, "end": v(160.01, -107.38) * mm});
            skArc(sketch, "E319", {"start": v(160.01, -107.38) * mm, "mid": v(162.76, -98.04) * mm, "end": v(165.4, -88.67) * mm});
            skArc(sketch, "E320", {"start": v(165.4, -88.67) * mm, "mid": v(168.83, -76.28) * mm, "end": v(172.3, -63.9) * mm});
            skArc(sketch, "E321", {"start": v(172.3, -63.9) * mm, "mid": v(174.36, -56.82) * mm, "end": v(176.54, -49.78) * mm});
            skArc(sketch, "E322", {"start": v(176.54, -49.78) * mm, "mid": v(178.32, -44.4) * mm, "end": v(180.24, -39.07) * mm});
            skArc(sketch, "E323", {"start": v(180.24, -39.07) * mm, "mid": v(182.44, -33.37) * mm, "end": v(184.76, -27.72) * mm});
            skArc(sketch, "E324", {"start": v(184.76, -27.72) * mm, "mid": v(187.36, -21.46) * mm, "end": v(189.87, -15.16) * mm});
            skArc(sketch, "E325", {"start": v(189.87, -15.16) * mm, "mid": v(191.38, -11.04) * mm, "end": v(192.7, -6.85) * mm});
            skArc(sketch, "E326", {"start": v(192.7, -6.85) * mm, "mid": v(193.53, -3.63) * mm, "end": v(194.14, -0.35) * mm});
            skArc(sketch, "E327", {"start": v(194.14, -0.35) * mm, "mid": v(194.49, 2.77) * mm, "end": v(194.58, 5.9) * mm});
            skArc(sketch, "E328", {"start": v(194.58, 5.9) * mm, "mid": v(193.95, 12.1) * mm, "end": v(192.18, 18.07) * mm});
            skArc(sketch, "E329", {"start": v(192.18, 18.07) * mm, "mid": v(189.3, 23.8) * mm, "end": v(185.49, 28.95) * mm});
            skArc(sketch, "E330", {"start": v(185.49, 28.95) * mm, "mid": v(180.89, 33.34) * mm, "end": v(175.6, 36.89) * mm});
            skArc(sketch, "E331", {"start": v(175.6, 36.89) * mm, "mid": v(169.99, 39.32) * mm, "end": v(164.01, 40.62) * mm});
            skArc(sketch, "E332", {"start": v(164.01, 40.62) * mm, "mid": v(162.95, 40.77) * mm, "end": v(161.9, 40.99) * mm});
            skArc(sketch, "E333", {"start": v(161.9, 40.99) * mm, "mid": v(160.88, 41.25) * mm, "end": v(159.89, 41.57) * mm});
            skArc(sketch, "E334", {"start": v(159.89, 41.57) * mm, "mid": v(159.03, 41.9) * mm, "end": v(158.2, 42.29) * mm});
            skArc(sketch, "E335", {"start": v(158.2, 42.29) * mm, "mid": v(157.64, 42.63) * mm, "end": v(157.13, 43.06) * mm});
            skArc(sketch, "E336", {"start": v(157.13, 43.06) * mm, "mid": v(156.24, 43.8) * mm, "end": v(155.22, 44.36) * mm});
            skArc(sketch, "E337", {"start": v(155.22, 44.36) * mm, "mid": v(154.12, 44.7) * mm, "end": v(152.98, 44.83) * mm});
            skArc(sketch, "E338", {"start": v(152.98, 44.83) * mm, "mid": v(151.87, 44.73) * mm, "end": v(150.8, 44.4) * mm});
            skArc(sketch, "E339", {"start": v(150.8, 44.4) * mm, "mid": v(149.86, 43.88) * mm, "end": v(149.06, 43.15) * mm});
            skArc(sketch, "E340", {"start": v(149.06, 43.15) * mm, "mid": v(148.64, 42.64) * mm, "end": v(148.27, 42.09) * mm});
            skArc(sketch, "E341", {"start": v(148.27, 42.09) * mm, "mid": v(147.64, 41.05) * mm, "end": v(147.02, 40) * mm});
            skArc(sketch, "E342", {"start": v(147.02, 40) * mm, "mid": v(146.32, 38.77) * mm, "end": v(145.64, 37.52) * mm});
            skArc(sketch, "E343", {"start": v(145.64, 37.52) * mm, "mid": v(144.95, 36.21) * mm, "end": v(144.29, 34.9) * mm});
            skArc(sketch, "E344", {"start": v(144.29, 34.9) * mm, "mid": v(143.47, 33.28) * mm, "end": v(142.61, 31.67) * mm});
            skArc(sketch, "E345", {"start": v(142.61, 31.67) * mm, "mid": v(141.38, 29.42) * mm, "end": v(140.12, 27.17) * mm});
            skArc(sketch, "E346", {"start": v(140.12, 27.17) * mm, "mid": v(138.74, 24.72) * mm, "end": v(137.34, 22.28) * mm});
            skArc(sketch, "E347", {"start": v(137.34, 22.28) * mm, "mid": v(136, 19.99) * mm, "end": v(134.65, 17.7) * mm});
            skLineSegment(sketch, "E348", {"start": v(134.65, 17.7) * mm, "end": v(128.23, 7.01) * mm});
            skLineSegment(sketch, "E349", {"start": v(128.23, 7.01) * mm, "end": v(121.82, 11.49) * mm});
            skArc(sketch, "E350", {"start": v(121.82, 11.49) * mm, "mid": v(118.3, 13.82) * mm, "end": v(114.64, 15.96) * mm});
            skArc(sketch, "E351", {"start": v(114.64, 15.96) * mm, "mid": v(110.22, 18.3) * mm, "end": v(105.73, 20.5) * mm});
            skArc(sketch, "E352", {"start": v(105.73, 20.5) * mm, "mid": v(101.18, 22.54) * mm, "end": v(96.56, 24.44) * mm});
            skArc(sketch, "E353", {"start": v(96.56, 24.44) * mm, "mid": v(92.64, 25.85) * mm, "end": v(88.65, 27.05) * mm});
            skArc(sketch, "E354", {"start": v(88.65, 27.05) * mm, "mid": v(84.75, 27.93) * mm, "end": v(80.8, 28.49) * mm});
            skArc(sketch, "E355", {"start": v(80.8, 28.49) * mm, "mid": v(75.16, 28.97) * mm, "end": v(69.5, 29.28) * mm});
            skArc(sketch, "E356", {"start": v(69.5, 29.28) * mm, "mid": v(63.88, 29.42) * mm, "end": v(58.25, 29.4) * mm});
            skArc(sketch, "E357", {"start": v(58.25, 29.4) * mm, "mid": v(54.4, 29.15) * mm, "end": v(50.58, 28.57) * mm});
            skArc(sketch, "E358", {"start": v(50.58, 28.57) * mm, "mid": v(49.3, 28.33) * mm, "end": v(48.03, 28.13) * mm});
            skArc(sketch, "E359", {"start": v(48.03, 28.13) * mm, "mid": v(47.48, 28.11) * mm, "end": v(46.93, 28.22) * mm});
            skArc(sketch, "E360", {"start": v(46.93, 28.22) * mm, "mid": v(46.56, 28.43) * mm, "end": v(46.3, 28.77) * mm});
            skArc(sketch, "E361", {"start": v(46.3, 28.77) * mm, "mid": v(46.06, 29.4) * mm, "end": v(45.88, 30.07) * mm});
            skArc(sketch, "E362", {"start": v(45.88, 30.07) * mm, "mid": v(45.72, 30.87) * mm, "end": v(45.56, 31.68) * mm});
            skArc(sketch, "E363", {"start": v(45.56, 31.68) * mm, "mid": v(45.03, 34.42) * mm, "end": v(44.5, 37.15) * mm});
            skArc(sketch, "E364", {"start": v(44.5, 37.15) * mm, "mid": v(43.86, 40.4) * mm, "end": v(43.24, 43.64) * mm});
            skArc(sketch, "E365", {"start": v(43.24, 43.64) * mm, "mid": v(42.54, 47.27) * mm, "end": v(41.84, 50.9) * mm});
            skArc(sketch, "E366", {"start": v(41.84, 50.9) * mm, "mid": v(41.14, 54.52) * mm, "end": v(40.43, 58.13) * mm});
            skArc(sketch, "E367", {"start": v(40.43, 58.13) * mm, "mid": v(39.8, 61.35) * mm, "end": v(39.16, 64.56) * mm});
            skArc(sketch, "E368", {"start": v(39.16, 64.56) * mm, "mid": v(38.62, 67.27) * mm, "end": v(38.07, 69.98) * mm});
            skArc(sketch, "E369", {"start": v(38.07, 69.98) * mm, "mid": v(37.91, 70.7) * mm, "end": v(37.73, 71.42) * mm});
            skArc(sketch, "E370", {"start": v(37.73, 71.42) * mm, "mid": v(37.63, 71.95) * mm, "end": v(37.6, 72.5) * mm});
            skArc(sketch, "E371", {"start": v(37.6, 72.5) * mm, "mid": v(37.71, 72.85) * mm, "end": v(37.97, 73.1) * mm});
            skArc(sketch, "E372", {"start": v(37.97, 73.1) * mm, "mid": v(38.44, 73.32) * mm, "end": v(38.94, 73.42) * mm});
            skArc(sketch, "E373", {"start": v(38.94, 73.42) * mm, "mid": v(40.1, 73.5) * mm, "end": v(41.26, 73.54) * mm});
            skArc(sketch, "E374", {"start": v(41.26, 73.54) * mm, "mid": v(45.23, 74) * mm, "end": v(49.07, 75.14) * mm});
            skArc(sketch, "E375", {"start": v(49.07, 75.14) * mm, "mid": v(52.74, 76.95) * mm, "end": v(56.07, 79.34) * mm});
            skArc(sketch, "E376", {"start": v(56.07, 79.34) * mm, "mid": v(59.12, 82.38) * mm, "end": v(61.67, 85.85) * mm});
            skArc(sketch, "E377", {"start": v(61.67, 85.85) * mm, "mid": v(63.82, 89.85) * mm, "end": v(65.42, 94.1) * mm});
            skArc(sketch, "E378", {"start": v(65.42, 94.1) * mm, "mid": v(66.96, 101.84) * mm, "end": v(66.95, 109.71) * mm});
            skArc(sketch, "E379", {"start": v(66.95, 109.71) * mm, "mid": v(65.37, 117.13) * mm, "end": v(62.2, 124.02) * mm});
            skArc(sketch, "E380", {"start": v(62.2, 124.02) * mm, "mid": v(57.39, 130.46) * mm, "end": v(51.37, 135.78) * mm});
            skArc(sketch, "E381", {"start": v(51.37, 135.78) * mm, "mid": v(43.7, 140.49) * mm, "end": v(35.43, 144.02) * mm});
            skArc(sketch, "E382", {"start": v(35.43, 144.02) * mm, "mid": v(34.3, 144.4) * mm, "end": v(33.17, 144.74) * mm});
            skArc(sketch, "E383", {"start": v(33.17, 144.74) * mm, "mid": v(32.04, 145.06) * mm, "end": v(30.9, 145.35) * mm});
            skArc(sketch, "E384", {"start": v(30.9, 145.35) * mm, "mid": v(29.9, 145.58) * mm, "end": v(28.89, 145.78) * mm});
            skArc(sketch, "E385", {"start": v(28.89, 145.78) * mm, "mid": v(28.26, 145.87) * mm, "end": v(27.64, 145.9) * mm});
            skLineSegment(sketch, "E386", {"start": v(27.64, 145.9) * mm, "end": v(25.3, 145.9) * mm});
            skLineSegment(sketch, "E387", {"start": v(25.3, 145.9) * mm, "end": v(25.54, 163.78) * mm});
            skArc(sketch, "E388", {"start": v(25.54, 163.78) * mm, "mid": v(25.6, 169.14) * mm, "end": v(25.64, 174.49) * mm});
            skArc(sketch, "E389", {"start": v(25.64, 174.49) * mm, "mid": v(25.6, 176.85) * mm, "end": v(25.45, 179.2) * mm});
            skArc(sketch, "E390", {"start": v(25.45, 179.2) * mm, "mid": v(25.27, 180.57) * mm, "end": v(24.94, 181.92) * mm});
            skArc(sketch, "E391", {"start": v(24.94, 181.92) * mm, "mid": v(24.51, 182.9) * mm, "end": v(23.89, 183.78) * mm});
            skArc(sketch, "E392", {"start": v(23.89, 183.78) * mm, "mid": v(22.93, 184.62) * mm, "end": v(21.81, 185.22) * mm});
            skArc(sketch, "E393", {"start": v(21.81, 185.22) * mm, "mid": v(20.4, 185.65) * mm, "end": v(18.96, 185.87) * mm});
            skArc(sketch, "E394", {"start": v(18.96, 185.87) * mm, "mid": v(17.56, 185.86) * mm, "end": v(16.18, 185.62) * mm});
            skArc(sketch, "E395", {"start": v(16.18, 185.62) * mm, "mid": v(15.17, 185.19) * mm, "end": v(14.34, 184.46) * mm});
            skArc(sketch, "E396", {"start": v(-63.8, 28.98) * mm, "mid": v(-61.4, 26.29) * mm, "end": v(-59.51, 23.2) * mm});
            skArc(sketch, "E397", {"start": v(-59.51, 23.2) * mm, "mid": v(-57.65, 18.95) * mm, "end": v(-56.18, 14.56) * mm});
            skArc(sketch, "E398", {"start": v(-56.18, 14.56) * mm, "mid": v(-55.06, 9.94) * mm, "end": v(-54.35, 5.24) * mm});
            skArc(sketch, "E399", {"start": v(-54.35, 5.24) * mm, "mid": v(-54.2, 1.25) * mm, "end": v(-54.66, -2.72) * mm});
            skArc(sketch, "E400", {"start": v(-54.66, -2.72) * mm, "mid": v(-54.93, -3.8) * mm, "end": v(-55.34, -4.85) * mm});
            skArc(sketch, "E401", {"start": v(-55.34, -4.85) * mm, "mid": v(-56.19, -6.63) * mm, "end": v(-57.09, -8.4) * mm});
            skArc(sketch, "E402", {"start": v(-57.09, -8.4) * mm, "mid": v(-58.2, -10.45) * mm, "end": v(-59.38, -12.48) * mm});
            skArc(sketch, "E403", {"start": v(-59.38, -12.48) * mm, "mid": v(-60.67, -14.6) * mm, "end": v(-62, -16.67) * mm});
            skArc(sketch, "E404", {"start": v(-62, -16.67) * mm, "mid": v(-65.46, -22.08) * mm, "end": v(-68.78, -27.58) * mm});
            skArc(sketch, "E405", {"start": v(-68.78, -27.58) * mm, "mid": v(-72.4, -33.86) * mm, "end": v(-75.9, -40.2) * mm});
            skArc(sketch, "E406", {"start": v(-75.9, -40.2) * mm, "mid": v(-79.57, -47.13) * mm, "end": v(-83.13, -54.11) * mm});
            skArc(sketch, "E407", {"start": v(-83.13, -54.11) * mm, "mid": v(-86.74, -61.49) * mm, "end": v(-90.25, -68.92) * mm});
            skArc(sketch, "E408", {"start": v(-90.25, -68.92) * mm, "mid": v(-91.95, -72.57) * mm, "end": v(-93.64, -76.21) * mm});
            skArc(sketch, "E409", {"start": v(-93.64, -76.21) * mm, "mid": v(-95.54, -80.28) * mm, "end": v(-97.44, -84.35) * mm});
            skArc(sketch, "E410", {"start": v(-97.44, -84.35) * mm, "mid": v(-99.25, -88.22) * mm, "end": v(-101.06, -92.09) * mm});
            skArc(sketch, "E411", {"start": v(-101.06, -92.09) * mm, "mid": v(-102.46, -95.06) * mm, "end": v(-103.86, -98.03) * mm});
            skLineSegment(sketch, "E412", {"start": v(-103.86, -98.03) * mm, "end": v(-109.73, -110.45) * mm});
            skLineSegment(sketch, "E413", {"start": v(-109.73, -110.45) * mm, "end": v(-112.54, -106.03) * mm});
            skArc(sketch, "E414", {"start": v(-112.54, -106.03) * mm, "mid": v(-114.28, -103.54) * mm, "end": v(-116.23, -101.22) * mm});
            skArc(sketch, "E415", {"start": v(-116.23, -101.22) * mm, "mid": v(-118.6, -98.8) * mm, "end": v(-121.12, -96.53) * mm});
            skArc(sketch, "E416", {"start": v(-121.12, -96.53) * mm, "mid": v(-123.72, -94.47) * mm, "end": v(-126.46, -92.58) * mm});
            skArc(sketch, "E417", {"start": v(-126.46, -92.58) * mm, "mid": v(-128.92, -91.17) * mm, "end": v(-131.5, -90.03) * mm});
            skArc(sketch, "E418", {"start": v(-131.5, -90.03) * mm, "mid": v(-132.84, -89.56) * mm, "end": v(-134.2, -89.16) * mm});
            skArc(sketch, "E419", {"start": v(-134.2, -89.16) * mm, "mid": v(-135.92, -88.73) * mm, "end": v(-137.64, -88.34) * mm});
            skArc(sketch, "E420", {"start": v(-137.64, -88.34) * mm, "mid": v(-139.42, -88) * mm, "end": v(-141.21, -87.7) * mm});
            skArc(sketch, "E421", {"start": v(-141.21, -87.7) * mm, "mid": v(-142.79, -87.5) * mm, "end": v(-144.37, -87.35) * mm});
            skLineSegment(sketch, "E422", {"start": v(-144.37, -87.35) * mm, "end": v(-151.54, -86.85) * mm});
            skLineSegment(sketch, "E423", {"start": v(-151.54, -86.85) * mm, "end": v(-145.23, -77.72) * mm});
            skArc(sketch, "E424", {"start": v(-145.23, -77.72) * mm, "mid": v(-140.72, -71.05) * mm, "end": v(-136.35, -64.29) * mm});
            skArc(sketch, "E425", {"start": v(-136.35, -64.29) * mm, "mid": v(-128.02, -51.09) * mm, "end": v(-119.74, -37.86) * mm});
            skArc(sketch, "E426", {"start": v(-119.74, -37.86) * mm, "mid": v(-111.33, -24.32) * mm, "end": v(-102.98, -10.75) * mm});
            skArc(sketch, "E427", {"start": v(-102.98, -10.75) * mm, "mid": v(-97.23, -1.26) * mm, "end": v(-91.58, 8.3) * mm});
            skArc(sketch, "E428", {"start": v(-91.58, 8.3) * mm, "mid": v(-89.56, 11.7) * mm, "end": v(-87.5, 15.09) * mm});
            skArc(sketch, "E429", {"start": v(-87.5, 15.09) * mm, "mid": v(-85.53, 18.22) * mm, "end": v(-83.52, 21.33) * mm});
            skArc(sketch, "E430", {"start": v(-83.52, 21.33) * mm, "mid": v(-81.8, 23.92) * mm, "end": v(-80.03, 26.48) * mm});
            skArc(sketch, "E431", {"start": v(-80.03, 26.48) * mm, "mid": v(-79.15, 27.61) * mm, "end": v(-78.17, 28.65) * mm});
            skArc(sketch, "E432", {"start": v(-78.17, 28.65) * mm, "mid": v(-76.48, 30.02) * mm, "end": v(-74.62, 31.12) * mm});
            skArc(sketch, "E433", {"start": v(-74.62, 31.12) * mm, "mid": v(-72.82, 31.78) * mm, "end": v(-70.92, 32.03) * mm});
            skArc(sketch, "E434", {"start": v(-70.92, 32.03) * mm, "mid": v(-69.05, 31.86) * mm, "end": v(-67.26, 31.29) * mm});
            skArc(sketch, "E435", {"start": v(-67.26, 31.29) * mm, "mid": v(-65.43, 30.28) * mm, "end": v(-63.8, 28.98) * mm});
            skArc(sketch, "E436", {"start": v(165.5, 24.38) * mm, "mid": v(167.56, 22.81) * mm, "end": v(169.38, 20.98) * mm});
            skArc(sketch, "E437", {"start": v(169.38, 20.98) * mm, "mid": v(170.82, 19.03) * mm, "end": v(171.92, 16.87) * mm});
            skArc(sketch, "E438", {"start": v(171.92, 16.87) * mm, "mid": v(172.8, 14.25) * mm, "end": v(173.32, 11.54) * mm});
            skArc(sketch, "E439", {"start": v(173.32, 11.54) * mm, "mid": v(173.65, 7.98) * mm, "end": v(173.76, 4.4) * mm});
            skArc(sketch, "E440", {"start": v(173.76, 4.4) * mm, "mid": v(173.65, 0.67) * mm, "end": v(173.36, -3.05) * mm});
            skArc(sketch, "E441", {"start": v(173.36, -3.05) * mm, "mid": v(172.89, -6.44) * mm, "end": v(172.19, -9.8) * mm});
            skArc(sketch, "E442", {"start": v(172.19, -9.8) * mm, "mid": v(171.06, -14.02) * mm, "end": v(169.75, -18.2) * mm});
            skArc(sketch, "E443", {"start": v(169.75, -18.2) * mm, "mid": v(167.34, -25.22) * mm, "end": v(164.86, -32.22) * mm});
            skArc(sketch, "E444", {"start": v(164.86, -32.22) * mm, "mid": v(163.46, -36.2) * mm, "end": v(162.13, -40.2) * mm});
            skArc(sketch, "E445", {"start": v(162.13, -40.2) * mm, "mid": v(160.2, -46.19) * mm, "end": v(158.31, -52.19) * mm});
            skArc(sketch, "E446", {"start": v(158.31, -52.19) * mm, "mid": v(156.23, -58.9) * mm, "end": v(154.19, -65.6) * mm});
            skArc(sketch, "E447", {"start": v(154.19, -65.6) * mm, "mid": v(152.25, -72.1) * mm, "end": v(150.34, -78.6) * mm});
            skArc(sketch, "E448", {"start": v(150.34, -78.6) * mm, "mid": v(146.5, -91.72) * mm, "end": v(142.62, -104.82) * mm});
            skArc(sketch, "E449", {"start": v(142.62, -104.82) * mm, "mid": v(140.17, -112.76) * mm, "end": v(137.57, -120.65) * mm});
            skArc(sketch, "E450", {"start": v(137.57, -120.65) * mm, "mid": v(135.83, -125.64) * mm, "end": v(134, -130.6) * mm});
            skArc(sketch, "E451", {"start": v(134, -130.6) * mm, "mid": v(133.37, -131.03) * mm, "end": v(132.74, -130.6) * mm});
            skArc(sketch, "E452", {"start": v(132.74, -130.6) * mm, "mid": v(130.9, -126.2) * mm, "end": v(128.85, -121.9) * mm});
            skArc(sketch, "E453", {"start": v(128.85, -121.9) * mm, "mid": v(126.81, -118.19) * mm, "end": v(124.51, -114.64) * mm});
            skArc(sketch, "E454", {"start": v(124.51, -114.64) * mm, "mid": v(122.14, -111.5) * mm, "end": v(119.53, -108.56) * mm});
            skArc(sketch, "E455", {"start": v(119.53, -108.56) * mm, "mid": v(116.73, -105.85) * mm, "end": v(113.73, -103.37) * mm});
            skArc(sketch, "E456", {"start": v(113.73, -103.37) * mm, "mid": v(111.62, -101.88) * mm, "end": v(109.4, -100.55) * mm});
            skArc(sketch, "E457", {"start": v(109.4, -100.55) * mm, "mid": v(106.97, -99.3) * mm, "end": v(104.46, -98.2) * mm});
            skArc(sketch, "E458", {"start": v(104.46, -98.2) * mm, "mid": v(102.06, -97.33) * mm, "end": v(99.61, -96.61) * mm});
            skArc(sketch, "E459", {"start": v(99.61, -96.61) * mm, "mid": v(97.63, -96.23) * mm, "end": v(95.6, -96.1) * mm});
            skArc(sketch, "E460", {"start": v(95.6, -96.1) * mm, "mid": v(95.16, -96.09) * mm, "end": v(94.72, -96.05) * mm});
            skArc(sketch, "E461", {"start": v(94.72, -96.05) * mm, "mid": v(94.34, -95.99) * mm, "end": v(93.97, -95.9) * mm});
            skArc(sketch, "E462", {"start": v(93.97, -95.9) * mm, "mid": v(93.7, -95.8) * mm, "end": v(93.45, -95.67) * mm});
            skArc(sketch, "E463", {"start": v(93.45, -95.67) * mm, "mid": v(93.33, -95.56) * mm, "end": v(93.3, -95.4) * mm});
            skArc(sketch, "E464", {"start": v(93.3, -95.4) * mm, "mid": v(93.32, -95.15) * mm, "end": v(93.4, -94.91) * mm});
            skArc(sketch, "E465", {"start": v(93.4, -94.91) * mm, "mid": v(93.99, -93.65) * mm, "end": v(94.58, -92.4) * mm});
            skArc(sketch, "E466", {"start": v(94.58, -92.4) * mm, "mid": v(95.28, -90.94) * mm, "end": v(96, -89.48) * mm});
            skArc(sketch, "E467", {"start": v(96, -89.48) * mm, "mid": v(96.84, -87.82) * mm, "end": v(97.68, -86.15) * mm});
            skArc(sketch, "E468", {"start": v(97.68, -86.15) * mm, "mid": v(98.7, -84.13) * mm, "end": v(99.7, -82.1) * mm});
            skArc(sketch, "E469", {"start": v(99.7, -82.1) * mm, "mid": v(100.95, -79.5) * mm, "end": v(102.18, -76.88) * mm});
            skArc(sketch, "E470", {"start": v(102.18, -76.88) * mm, "mid": v(103.44, -74.16) * mm, "end": v(104.68, -71.44) * mm});
            skArc(sketch, "E471", {"start": v(104.68, -71.44) * mm, "mid": v(105.76, -69.02) * mm, "end": v(106.82, -66.6) * mm});
            skArc(sketch, "E472", {"start": v(106.82, -66.6) * mm, "mid": v(109.57, -60.36) * mm, "end": v(112.43, -54.16) * mm});
            skArc(sketch, "E473", {"start": v(112.43, -54.16) * mm, "mid": v(115.31, -48.18) * mm, "end": v(118.3, -42.25) * mm});
            skArc(sketch, "E474", {"start": v(118.3, -42.25) * mm, "mid": v(121.51, -36.13) * mm, "end": v(124.83, -30.07) * mm});
            skArc(sketch, "E475", {"start": v(124.83, -30.07) * mm, "mid": v(128.6, -23.42) * mm, "end": v(132.44, -16.83) * mm});
            skArc(sketch, "E476", {"start": v(132.44, -16.83) * mm, "mid": v(135.98, -10.76) * mm, "end": v(139.44, -4.64) * mm});
            skArc(sketch, "E477", {"start": v(139.44, -4.64) * mm, "mid": v(142.76, 1.43) * mm, "end": v(146, 7.56) * mm});
            skArc(sketch, "E478", {"start": v(146, 7.56) * mm, "mid": v(148.73, 12.9) * mm, "end": v(151.39, 18.26) * mm});
            skArc(sketch, "E479", {"start": v(151.39, 18.26) * mm, "mid": v(152.85, 21.52) * mm, "end": v(154.12, 24.85) * mm});
            skArc(sketch, "E480", {"start": v(154.12, 24.85) * mm, "mid": v(154.49, 25.82) * mm, "end": v(154.9, 26.76) * mm});
            skArc(sketch, "E481", {"start": v(154.9, 26.76) * mm, "mid": v(155.19, 27.2) * mm, "end": v(155.6, 27.55) * mm});
            skArc(sketch, "E482", {"start": v(155.6, 27.55) * mm, "mid": v(156.08, 27.74) * mm, "end": v(156.6, 27.78) * mm});
            skArc(sketch, "E483", {"start": v(156.6, 27.78) * mm, "mid": v(157.56, 27.67) * mm, "end": v(158.52, 27.5) * mm});
            skArc(sketch, "E484", {"start": v(158.52, 27.5) * mm, "mid": v(159.28, 27.32) * mm, "end": v(160.03, 27.08) * mm});
            skArc(sketch, "E485", {"start": v(160.03, 27.08) * mm, "mid": v(160.97, 26.72) * mm, "end": v(161.9, 26.32) * mm});
            skArc(sketch, "E486", {"start": v(161.9, 26.32) * mm, "mid": v(162.88, 25.86) * mm, "end": v(163.83, 25.37) * mm});
            skArc(sketch, "E487", {"start": v(163.83, 25.37) * mm, "mid": v(164.68, 24.9) * mm, "end": v(165.5, 24.38) * mm});
            skArc(sketch, "E488", {"start": v(-140.07, -105.63) * mm, "mid": v(-136.72, -107.57) * mm, "end": v(-133.69, -109.97) * mm});
            skArc(sketch, "E489", {"start": v(-133.69, -109.97) * mm, "mid": v(-130.5, -113.17) * mm, "end": v(-127.62, -116.64) * mm});
            skArc(sketch, "E490", {"start": v(-127.62, -116.64) * mm, "mid": v(-125.2, -120.16) * mm, "end": v(-123.13, -123.9) * mm});
            skArc(sketch, "E491", {"start": v(-123.13, -123.9) * mm, "mid": v(-122.07, -126.82) * mm, "end": v(-121.7, -129.92) * mm});
            skArc(sketch, "E492", {"start": v(-121.7, -129.92) * mm, "mid": v(-121.97, -131.78) * mm, "end": v(-122.74, -133.5) * mm});
            skArc(sketch, "E493", {"start": v(-122.74, -133.5) * mm, "mid": v(-125.04, -137.04) * mm, "end": v(-127.46, -140.51) * mm});
            skArc(sketch, "E494", {"start": v(-127.46, -140.51) * mm, "mid": v(-130.19, -144.14) * mm, "end": v(-133.07, -147.65) * mm});
            skArc(sketch, "E495", {"start": v(-133.07, -147.65) * mm, "mid": v(-135.63, -150.44) * mm, "end": v(-138.39, -153.05) * mm});
            skArc(sketch, "E496", {"start": v(-138.39, -153.05) * mm, "mid": v(-141.27, -155.28) * mm, "end": v(-144.42, -157.13) * mm});
            skArc(sketch, "E497", {"start": v(-144.42, -157.13) * mm, "mid": v(-147.64, -158.46) * mm, "end": v(-151.01, -159.31) * mm});
            skArc(sketch, "E498", {"start": v(-151.01, -159.31) * mm, "mid": v(-154.33, -159.63) * mm, "end": v(-157.65, -159.43) * mm});
            skArc(sketch, "E499", {"start": v(-157.65, -159.43) * mm, "mid": v(-160.83, -158.72) * mm, "end": v(-163.84, -157.5) * mm});
            skArc(sketch, "E500", {"start": v(-163.84, -157.5) * mm, "mid": v(-165.6, -156.44) * mm, "end": v(-167.17, -155.14) * mm});
            skArc(sketch, "E501", {"start": v(-167.17, -155.14) * mm, "mid": v(-169.07, -153.18) * mm, "end": v(-170.84, -151.1) * mm});
            skArc(sketch, "E502", {"start": v(-170.84, -151.1) * mm, "mid": v(-172.49, -148.89) * mm, "end": v(-174, -146.58) * mm});
            skArc(sketch, "E503", {"start": v(-174, -146.58) * mm, "mid": v(-174.98, -144.68) * mm, "end": v(-175.7, -142.66) * mm});
            skArc(sketch, "E504", {"start": v(-175.7, -142.66) * mm, "mid": v(-176.35, -139.69) * mm, "end": v(-176.7, -136.66) * mm});
            skArc(sketch, "E505", {"start": v(-176.7, -136.66) * mm, "mid": v(-176.73, -133.4) * mm, "end": v(-176.49, -130.14) * mm});
            skArc(sketch, "E506", {"start": v(-176.49, -130.14) * mm, "mid": v(-175.95, -126.84) * mm, "end": v(-175.13, -123.6) * mm});
            skArc(sketch, "E507", {"start": v(-175.13, -123.6) * mm, "mid": v(-174.04, -120.51) * mm, "end": v(-172.68, -117.53) * mm});
            skArc(sketch, "E508", {"start": v(-172.68, -117.53) * mm, "mid": v(-169.87, -112.92) * mm, "end": v(-166.43, -108.77) * mm});
            skArc(sketch, "E509", {"start": v(-166.43, -108.77) * mm, "mid": v(-162.86, -105.81) * mm, "end": v(-158.72, -103.74) * mm});
            skArc(sketch, "E510", {"start": v(-158.72, -103.74) * mm, "mid": v(-154.33, -102.7) * mm, "end": v(-149.82, -102.73) * mm});
            skArc(sketch, "E511", {"start": v(-149.82, -102.73) * mm, "mid": v(-144.82, -103.78) * mm, "end": v(-140.07, -105.63) * mm});
            skArc(sketch, "E512", {"start": v(103.52, -113.7) * mm, "mid": v(105.42, -115.2) * mm, "end": v(107.16, -116.88) * mm});
            skArc(sketch, "E513", {"start": v(107.16, -116.88) * mm, "mid": v(108.98, -118.96) * mm, "end": v(110.67, -121.17) * mm});
            skArc(sketch, "E514", {"start": v(110.67, -121.17) * mm, "mid": v(112.33, -123.67) * mm, "end": v(113.83, -126.27) * mm});
            skArc(sketch, "E515", {"start": v(113.83, -126.27) * mm, "mid": v(115.21, -129.03) * mm, "end": v(116.43, -131.86) * mm});
            skArc(sketch, "E516", {"start": v(116.43, -131.86) * mm, "mid": v(117.04, -133.53) * mm, "end": v(117.56, -135.23) * mm});
            skArc(sketch, "E517", {"start": v(117.56, -135.23) * mm, "mid": v(117.96, -136.83) * mm, "end": v(118.25, -138.46) * mm});
            skArc(sketch, "E518", {"start": v(118.25, -138.46) * mm, "mid": v(118.48, -140.36) * mm, "end": v(118.62, -142.27) * mm});
            skArc(sketch, "E519", {"start": v(118.62, -142.27) * mm, "mid": v(118.7, -144.94) * mm, "end": v(118.75, -147.6) * mm});
            skArc(sketch, "E520", {"start": v(118.75, -147.6) * mm, "mid": v(118.74, -150.48) * mm, "end": v(118.7, -153.36) * mm});
            skArc(sketch, "E521", {"start": v(118.7, -153.36) * mm, "mid": v(118.6, -154.92) * mm, "end": v(118.4, -156.46) * mm});
            skArc(sketch, "E522", {"start": v(118.4, -156.46) * mm, "mid": v(118.14, -157.58) * mm, "end": v(117.74, -158.65) * mm});
            skArc(sketch, "E523", {"start": v(117.74, -158.65) * mm, "mid": v(117.17, -159.76) * mm, "end": v(116.5, -160.8) * mm});
            skArc(sketch, "E524", {"start": v(116.5, -160.8) * mm, "mid": v(115.07, -162.47) * mm, "end": v(113.37, -163.85) * mm});
            skArc(sketch, "E525", {"start": v(113.37, -163.85) * mm, "mid": v(110.64, -165.57) * mm, "end": v(107.81, -167.13) * mm});
            skArc(sketch, "E526", {"start": v(107.81, -167.13) * mm, "mid": v(104.9, -168.5) * mm, "end": v(101.93, -169.7) * mm});
            skArc(sketch, "E527", {"start": v(101.93, -169.7) * mm, "mid": v(99.87, -170.25) * mm, "end": v(97.75, -170.4) * mm});
            skArc(sketch, "E528", {"start": v(97.75, -170.4) * mm, "mid": v(94.51, -169.94) * mm, "end": v(91.46, -168.8) * mm});
            skArc(sketch, "E529", {"start": v(91.46, -168.8) * mm, "mid": v(87.9, -166.72) * mm, "end": v(84.6, -164.27) * mm});
            skArc(sketch, "E530", {"start": v(84.6, -164.27) * mm, "mid": v(81.3, -161.2) * mm, "end": v(78.32, -157.79) * mm});
            skArc(sketch, "E531", {"start": v(78.32, -157.79) * mm, "mid": v(75.8, -154.17) * mm, "end": v(73.68, -150.28) * mm});
            skArc(sketch, "E532", {"start": v(73.68, -150.28) * mm, "mid": v(72.23, -146.37) * mm, "end": v(71.46, -142.26) * mm});
            skArc(sketch, "E533", {"start": v(71.46, -142.26) * mm, "mid": v(71.34, -137.81) * mm, "end": v(71.84, -133.4) * mm});
            skArc(sketch, "E534", {"start": v(71.84, -133.4) * mm, "mid": v(73, -128.94) * mm, "end": v(74.76, -124.68) * mm});
            skArc(sketch, "E535", {"start": v(74.76, -124.68) * mm, "mid": v(77.08, -120.7) * mm, "end": v(79.93, -117.08) * mm});
            skArc(sketch, "E536", {"start": v(79.93, -117.08) * mm, "mid": v(80.76, -116.19) * mm, "end": v(81.63, -115.34) * mm});
            skArc(sketch, "E537", {"start": v(81.63, -115.34) * mm, "mid": v(82.57, -114.48) * mm, "end": v(83.54, -113.65) * mm});
            skArc(sketch, "E538", {"start": v(83.54, -113.65) * mm, "mid": v(84.44, -112.93) * mm, "end": v(85.37, -112.25) * mm});
            skArc(sketch, "E539", {"start": v(85.37, -112.25) * mm, "mid": v(86.06, -111.8) * mm, "end": v(86.8, -111.43) * mm});
            skArc(sketch, "E540", {"start": v(86.8, -111.43) * mm, "mid": v(88.66, -110.76) * mm, "end": v(90.6, -110.41) * mm});
            skArc(sketch, "E541", {"start": v(90.6, -110.41) * mm, "mid": v(92.85, -110.33) * mm, "end": v(95.1, -110.5) * mm});
            skArc(sketch, "E542", {"start": v(95.1, -110.5) * mm, "mid": v(97.38, -110.95) * mm, "end": v(99.6, -111.64) * mm});
            skArc(sketch, "E543", {"start": v(99.6, -111.64) * mm, "mid": v(101.63, -112.55) * mm, "end": v(103.52, -113.7) * mm});
            skSolve(sketch);
        }
        {
            var Q0;
            Q0=qSketchRegion(id+"F3",true);
            var Q1;
            Q1=sQuery(id+"F3.wireOp",EDGE,"c928f899-12af-4b01-b412-b3b7da3d830f");
            var Q2;
            Q2=sQuery(id+"F3.wireOp",EDGE,"b69f99c7-a6d0-4d1b-8752-9e82ab4c99ec");
            extrude(context, id + "F4", {"entities" : qUnion([Q0]), "operationType" : NewBodyOperationType.ADD, "surfaceEntities" : qUnion([Q1, Q2]), "depth" : 350 * mm});
        }
        {
            var Q0;
            Q0=makeQuery(id+"F4.opExtrude","SWEPT_BODY",BODY,{"disambiguationData":[OSD([sQuery(id+"F3.wireOp",EDGE,"15c6da4e-992d-4824-9d20-70d2d6be9970"),sQuery(id+"F3.wireOp",EDGE,"268c69ec-46be-456f-85eb-69decc32fe39"),sQuery(id+"F3.wireOp",EDGE,"1d386307-6059-4203-bca6-0c1cec3c82e1"),sQuery(id+"F3.wireOp",EDGE,"7d7c66d2-f869-427f-806b-ad436cacd60e"),sQuery(id+"F3.wireOp",EDGE,"1db91850-860e-493f-a3af-7a0f3f1512ae"),sQuery(id+"F3.wireOp",EDGE,"2c65f23b-9f03-4f6f-ab37-de452af29e3c"),sQuery(id+"F3.wireOp",EDGE,"ba006cbc-bbd7-44d9-84cc-9cde0967c280"),sQuery(id+"F3.wireOp",EDGE,"ae950208-c781-4a25-8fcf-ffe59b9085ff"),sQuery(id+"F3.wireOp",EDGE,"3cce0944-c62d-4831-9b9d-d1a418d328b4"),sQuery(id+"F3.wireOp",EDGE,"9edc5e7d-16c0-40c4-98ad-6b91d5df0e78"),sQuery(id+"F3.wireOp",EDGE,"aa452f44-44a2-4c64-bff5-a2a639df00db"),sQuery(id+"F3.wireOp",EDGE,"16259f99-ce20-4b7b-81e1-fa0909c03eb4"),sQuery(id+"F3.wireOp",EDGE,"79895566-a943-429d-b257-d76af3645bdf"),sQuery(id+"F3.wireOp",EDGE,"a85490ef-f17e-45c8-b92b-28215162778a"),sQuery(id+"F3.wireOp",EDGE,"322f1036-a6fd-4992-ab69-5919540af7a6"),sQuery(id+"F3.wireOp",EDGE,"0a87ff38-4ab4-4140-b3c3-2d7501d9f3b1"),sQuery(id+"F3.wireOp",EDGE,"a6e7bdf2-ef3e-49d4-9b3c-e34f5a41e0c4"),sQuery(id+"F3.wireOp",EDGE,"3e588790-576f-47c1-9730-f5e27fa1e8f9"),sQuery(id+"F3.wireOp",EDGE,"ce3739ef-15fd-4754-ad9c-ccf511a9a8fb"),sQuery(id+"F3.wireOp",EDGE,"201134a3-66f3-4a3f-aa9b-76948966efc0"),sQuery(id+"F3.wireOp",EDGE,"65b511ea-0759-428d-8070-88e1f521d8ea"),sQuery(id+"F3.wireOp",EDGE,"c37cddb6-5cf8-4891-aff4-7191a72080b9"),sQuery(id+"F3.wireOp",EDGE,"52a43dbd-e952-43e1-be3d-d70e107260e6"),sQuery(id+"F3.wireOp",EDGE,"08c1271f-f5c3-4f26-be27-7f5e21217dff"),sQuery(id+"F3.wireOp",EDGE,"59a09f58-0503-4180-962a-e04db21f0da8"),sQuery(id+"F3.wireOp",EDGE,"e56a4626-e956-42c3-bb5d-cd9dae1ca801"),sQuery(id+"F3.wireOp",EDGE,"5ff5d55f-af90-49eb-8040-353101557de8"),sQuery(id+"F3.wireOp",EDGE,"0ed7430b-e164-4f56-8af9-4534524aa7c0"),sQuery(id+"F3.wireOp",EDGE,"b5610a6e-b6bb-43e3-9a8d-d3d7c5f0098b"),sQuery(id+"F3.wireOp",EDGE,"1d417af8-88ad-47c2-a4e2-6fec82bd6695"),sQuery(id+"F3.wireOp",EDGE,"778ae99a-956a-4ddb-8078-d9bc57f9fc8e"),sQuery(id+"F3.wireOp",EDGE,"5b19af09-f144-446e-9dfa-8766819c9efd"),sQuery(id+"F3.wireOp",EDGE,"028339f6-0475-4a57-af8d-550e32ad7466"),sQuery(id+"F3.wireOp",EDGE,"d5ae35b6-d210-433a-92c8-e92622696872"),sQuery(id+"F3.wireOp",EDGE,"16a2e606-2caa-4876-9ffa-8f08c4ff3a37"),sQuery(id+"F3.wireOp",EDGE,"5b90b144-be56-4de7-a9dd-c1e0336acbe3"),sQuery(id+"F3.wireOp",EDGE,"5912d126-c5fc-41e4-bfb8-b4fefc52ca72"),sQuery(id+"F3.wireOp",EDGE,"2e96ce95-bd3e-4f27-a7f8-b62cf5efe954"),sQuery(id+"F3.wireOp",EDGE,"ecb4e259-1207-4dd0-bc3c-87c6506cc3a5"),sQuery(id+"F3.wireOp",EDGE,"105fb72e-4d79-4204-af2f-b3b26f5eb8d1"),sQuery(id+"F3.wireOp",EDGE,"fa59b598-df54-48c6-bb8f-c5f7618c69d0"),sQuery(id+"F3.wireOp",EDGE,"a6beef0d-f124-47ac-b957-e6cd3057a354"),sQuery(id+"F3.wireOp",EDGE,"7c3eaf53-dcb7-43b1-ad18-80ff953eb59e"),sQuery(id+"F3.wireOp",EDGE,"281fe206-104f-408f-94b6-be79f12604c9")])]});
            var Q1;
            Q1=makeQuery(id+"F4.opExtrude","SWEPT_BODY",BODY,{"disambiguationData":[OSD([sQuery(id+"F3.wireOp",EDGE,"58f6206a-5554-41d4-8cf7-6e0b4724a469"),sQuery(id+"F3.wireOp",EDGE,"85dabe77-b6aa-43d5-a519-64383616f71e"),sQuery(id+"F3.wireOp",EDGE,"4b679fe6-9e11-497d-b8fd-14ca14e49ddd"),sQuery(id+"F3.wireOp",EDGE,"51de25f6-d59e-4805-a327-1fd7e38869c8"),sQuery(id+"F3.wireOp",EDGE,"d47977fb-70d3-4df8-bc35-66fcc0e556e0"),sQuery(id+"F3.wireOp",EDGE,"235006b0-8f14-4ca2-82f0-f96b6b8c4766"),sQuery(id+"F3.wireOp",EDGE,"0fc7acd6-1c1d-47a8-ba12-62eb658d35ca"),sQuery(id+"F3.wireOp",EDGE,"883fa5e3-ca4c-4ce6-a249-4debf538fe24"),sQuery(id+"F3.wireOp",EDGE,"1da09ed1-22d9-43a1-a655-8acff5d61309"),sQuery(id+"F3.wireOp",EDGE,"32654a82-a09a-444f-bf73-45f818f0f235"),sQuery(id+"F3.wireOp",EDGE,"a398fd80-a0a9-4724-ba0e-1a7a000baa92"),sQuery(id+"F3.wireOp",EDGE,"f39f97c8-53f5-4046-9905-b28daecd4f10"),sQuery(id+"F3.wireOp",EDGE,"2484d883-0ec2-4c7d-9023-165ebbef226c"),sQuery(id+"F3.wireOp",EDGE,"f026d96f-3d32-4113-a1c9-3545f5cdbe4a"),sQuery(id+"F3.wireOp",EDGE,"974fee18-719e-4620-aace-d3676da2011b"),sQuery(id+"F3.wireOp",EDGE,"0c5766d2-a026-45af-bffd-0d1f783d5157"),sQuery(id+"F3.wireOp",EDGE,"5da13fee-9c04-45d8-805f-c7a03dde2383"),sQuery(id+"F3.wireOp",EDGE,"dbea32a3-85bd-4957-aef2-b6fe64a02f6b"),sQuery(id+"F3.wireOp",EDGE,"fba134ea-bf40-4191-ad8f-cc6b2b040a97"),sQuery(id+"F3.wireOp",EDGE,"0c19e200-7cd5-4fcb-83ed-261bd7936bc7"),sQuery(id+"F3.wireOp",EDGE,"246b843b-ea86-44e5-9cb9-335e6677b61d"),sQuery(id+"F3.wireOp",EDGE,"c1b3c9bc-1eb4-4c9b-99c8-0cebed89395a"),sQuery(id+"F3.wireOp",EDGE,"f93eebc3-1447-4029-8362-91325193ac2b"),sQuery(id+"F3.wireOp",EDGE,"bf86b12d-53a9-4c19-abaa-b1e658933ceb"),sQuery(id+"F3.wireOp",EDGE,"89646a71-1a60-4e14-b80a-74fb601d0855"),sQuery(id+"F3.wireOp",EDGE,"7b03dcde-0a52-4f3c-80e9-110d1d805e93"),sQuery(id+"F3.wireOp",EDGE,"83e8d1f3-8820-485b-8b6d-3ecd79124883"),sQuery(id+"F3.wireOp",EDGE,"ec7b56eb-ca95-44fd-a774-e9b7f9d3f50d"),sQuery(id+"F3.wireOp",EDGE,"31861aa6-cfd1-43ce-a7c5-bacfb7e2a30f"),sQuery(id+"F3.wireOp",EDGE,"fa3de647-1dd9-4141-982b-74ae8d07851d"),sQuery(id+"F3.wireOp",EDGE,"75d7c1c5-761c-4178-bfd4-4f469045899b"),sQuery(id+"F3.wireOp",EDGE,"4b3d7518-bd5d-4ecc-b2c5-d8dd665de4f4"),sQuery(id+"F3.wireOp",EDGE,"3be2682d-01bd-4f31-9cde-9df16a01e4a9"),sQuery(id+"F3.wireOp",EDGE,"72d3c7a9-2794-46eb-9b0d-6c526cc1b9a3"),sQuery(id+"F3.wireOp",EDGE,"0137e336-6b26-4f8d-b9ad-47ce1aa9eb31"),sQuery(id+"F3.wireOp",EDGE,"96000e4a-2d86-4b9f-af7d-a1c875cc048c"),sQuery(id+"F3.wireOp",EDGE,"139c5a79-9c0f-4e15-b57f-4c09662495a3"),sQuery(id+"F3.wireOp",EDGE,"8ea04d8b-b3da-46bb-9742-d8cba6b23bda"),sQuery(id+"F3.wireOp",EDGE,"b352b580-467e-481c-88ac-6217b8462947"),sQuery(id+"F3.wireOp",EDGE,"2503a493-1722-4539-8d54-7329fc0b116a"),sQuery(id+"F3.wireOp",EDGE,"a0615e06-0a48-4c65-8818-f0f693937022"),sQuery(id+"F3.wireOp",EDGE,"08389002-1ce8-438a-b5a4-698ca33590c2"),sQuery(id+"F3.wireOp",EDGE,"1756e4aa-c30a-461e-962c-81ee35d31e55"),sQuery(id+"F3.wireOp",EDGE,"5f84c249-07ea-4efb-9be3-ca494937f772"),sQuery(id+"F3.wireOp",EDGE,"cbefd041-b54f-4587-87b6-437b2290d1fc"),sQuery(id+"F3.wireOp",EDGE,"d44f58d4-f1a7-4aec-b016-8e7f1e498aeb"),sQuery(id+"F3.wireOp",EDGE,"0a5be90b-7545-44ea-9f2d-c726a5a2121c"),sQuery(id+"F3.wireOp",EDGE,"0cfaa442-d102-4580-8ef6-489f2aa1e6b3")])]});
            var Q2;
            Q2=makeQuery(id+"F4.opExtrude","SWEPT_BODY",BODY,{"disambiguationData":[OSD([sQuery(id+"F3.wireOp",EDGE,"9cc7aec6-4d94-4577-ab6c-32f5aa316238"),sQuery(id+"F3.wireOp",EDGE,"5ab2d840-4a32-405a-8c4b-a8126e3e1bc1"),sQuery(id+"F3.wireOp",EDGE,"56de48b4-9620-4637-8196-310e2641530f"),sQuery(id+"F3.wireOp",EDGE,"55327826-e64b-4830-85f2-3f22d36f43b5"),sQuery(id+"F3.wireOp",EDGE,"0245b46f-a639-4a95-8ca3-1568736ceed2"),sQuery(id+"F3.wireOp",EDGE,"9bd8a002-6ca7-4c84-8984-a620eefad103"),sQuery(id+"F3.wireOp",EDGE,"d4736c5e-da0b-46a0-ba9d-17ae07bb2b66"),sQuery(id+"F3.wireOp",EDGE,"125695b8-77e6-4e99-8f78-5f8fae1a0c71"),sQuery(id+"F3.wireOp",EDGE,"c9f25b10-a495-4684-8f25-8f255fabab6e"),sQuery(id+"F3.wireOp",EDGE,"0dbee67a-2ab6-4abb-ae16-0fe64d623848"),sQuery(id+"F3.wireOp",EDGE,"92c08d8e-ed2e-41a3-9c1a-b5ddaf8a0bf1"),sQuery(id+"F3.wireOp",EDGE,"00fabb15-0c1e-492e-85c1-17390e5b12bc"),sQuery(id+"F3.wireOp",EDGE,"065a9352-dddb-4e3f-b02a-444c867b75fe"),sQuery(id+"F3.wireOp",EDGE,"ef206bb6-e4f2-4189-9fc7-a7823c329ad6"),sQuery(id+"F3.wireOp",EDGE,"7199cbbe-c9bf-4cb9-b928-2ff8a84eb09e"),sQuery(id+"F3.wireOp",EDGE,"17bf9ed1-b881-4f74-816d-3511b6b328c7"),sQuery(id+"F3.wireOp",EDGE,"e5b615d0-4193-495d-b285-bd69ae30f000"),sQuery(id+"F3.wireOp",EDGE,"cfeaf62f-6be1-426b-9732-01e1a667be7e"),sQuery(id+"F3.wireOp",EDGE,"ac56344b-5ee6-4fa5-8e47-65b2a4ea3a01"),sQuery(id+"F3.wireOp",EDGE,"45b5fa53-15fd-43a0-91b0-943cc3286fc9")])]});
            var Q3;
            Q3=makeQuery(id+"F4.opExtrude","SWEPT_BODY",BODY,{"disambiguationData":[OSD([sQuery(id+"F3.wireOp",EDGE,"7bdfe37d-9957-4663-8239-5490fd3220d9"),sQuery(id+"F3.wireOp",EDGE,"6a91314f-c002-4565-bbf8-bb9f29165fb8"),sQuery(id+"F3.wireOp",EDGE,"b69f99c7-a6d0-4d1b-8752-9e82ab4c99ec"),sQuery(id+"F3.wireOp",EDGE,"c928f899-12af-4b01-b412-b3b7da3d830f"),sQuery(id+"F3.wireOp",EDGE,"ffa58721-cdd5-406d-be26-d96f7a050df4"),sQuery(id+"F3.wireOp",EDGE,"02fc7fb8-293b-44ff-ab78-63506d0aedb9"),sQuery(id+"F3.wireOp",EDGE,"147fb6cb-2565-4fb5-9280-6afbf9eef36b"),sQuery(id+"F3.wireOp",EDGE,"2cee3704-4124-415a-b391-31af1cf305d7"),sQuery(id+"F3.wireOp",EDGE,"32b2fb71-03c8-4978-9d95-2b5aaf044d0d"),sQuery(id+"F3.wireOp",EDGE,"e5d05796-7d6c-4350-8a4e-d55f5ade2f77"),sQuery(id+"F3.wireOp",EDGE,"77b1164c-8dd4-4680-b616-ac151a422eb2"),sQuery(id+"F3.wireOp",EDGE,"ec0798b8-0fbb-49ea-9766-39d2ee0936b0"),sQuery(id+"F3.wireOp",EDGE,"c4af6478-2a03-47a6-862f-c0c71886b8a3"),sQuery(id+"F3.wireOp",EDGE,"1912a38f-fa28-45c6-ab33-84cac2787056"),sQuery(id+"F3.wireOp",EDGE,"5d79fa95-f66d-4d2b-923b-4d54735f1fbd"),sQuery(id+"F3.wireOp",EDGE,"2db7aef4-a710-4bcf-9c1c-a8a87719953d"),sQuery(id+"F3.wireOp",EDGE,"183449de-345c-4115-9bca-43a403e62dbd"),sQuery(id+"F3.wireOp",EDGE,"e3ac8c9b-cab5-44b0-ad81-0e2b680c384a"),sQuery(id+"F3.wireOp",EDGE,"92e85db6-f458-41f6-a9a1-1e1a1a7e7809"),sQuery(id+"F3.wireOp",EDGE,"f0dbb46f-43a9-447b-9c75-8dfc9b95470d"),sQuery(id+"F3.wireOp",EDGE,"4b73f5f6-f769-4414-bdba-7d253e58fff4"),sQuery(id+"F3.wireOp",EDGE,"a88669dc-35b3-46bb-964f-c9bf6c4ab898"),sQuery(id+"F3.wireOp",EDGE,"2c559bae-f38f-4377-91e6-3c9de70acf11"),sQuery(id+"F3.wireOp",EDGE,"c1caf99b-adaa-42fe-a319-8cbcd819cf89"),sQuery(id+"F3.wireOp",EDGE,"54b04dd4-0ec4-4956-b19c-1141095738e3"),sQuery(id+"F3.wireOp",EDGE,"098f7a84-b7b8-4879-b21a-5c38879e4110"),sQuery(id+"F3.wireOp",EDGE,"b406a8e6-a226-4f3d-ac30-e4d06e4dac62"),sQuery(id+"F3.wireOp",EDGE,"36f95d1d-68ce-4231-ad71-3960c85e5915"),sQuery(id+"F3.wireOp",EDGE,"dc12cad8-2eed-454e-aa74-30099b1c9064"),sQuery(id+"F3.wireOp",EDGE,"4c78a4fd-cd81-43d6-85d6-6e4d3fbc1e98"),sQuery(id+"F3.wireOp",EDGE,"ee9e30de-787b-4e8f-b425-43a8e9289f81"),sQuery(id+"F3.wireOp",EDGE,"2518a3a4-c96b-4463-8704-0b71c65c60d2"),sQuery(id+"F3.wireOp",EDGE,"c9129a67-398c-4e37-92cb-2d54ff2e2e82"),sQuery(id+"F3.wireOp",EDGE,"d429d547-9f5b-42c6-bcca-effad2fa908f"),sQuery(id+"F3.wireOp",EDGE,"99d16e94-b2b3-43d5-9c7b-7bd463994dcb"),sQuery(id+"F3.wireOp",EDGE,"32993909-9a70-47ee-9097-89fff220f839"),sQuery(id+"F3.wireOp",EDGE,"6eabbeed-9496-4825-b168-63782a34f495"),sQuery(id+"F3.wireOp",EDGE,"f74987e3-8e60-4a5b-857f-839ae8aaf0cf"),sQuery(id+"F3.wireOp",EDGE,"1c218c86-035d-4441-93c0-9621d3297c3a"),sQuery(id+"F3.wireOp",EDGE,"0133f513-4b11-4cc4-b075-4625e9591e41"),sQuery(id+"F3.wireOp",EDGE,"fe921ad4-a8f5-4772-9aeb-350aca2e8948"),sQuery(id+"F3.wireOp",EDGE,"bfde0a4f-3cec-4f8e-8a23-dd1441b34c2b"),sQuery(id+"F3.wireOp",EDGE,"b41521ff-c5df-4b64-83ed-5e7635cf4438"),sQuery(id+"F3.wireOp",EDGE,"ed692599-6bbb-4379-8e89-ea326a0a0f87"),sQuery(id+"F3.wireOp",EDGE,"a98451c0-d76c-436e-99f9-a3fe9c8430a4"),sQuery(id+"F3.wireOp",EDGE,"561965b2-3050-4f49-9305-d98a2b852bbe"),sQuery(id+"F3.wireOp",EDGE,"e13dfa59-48e6-4b4e-94b9-1fc5254b0f2e"),sQuery(id+"F3.wireOp",EDGE,"0354e106-253a-4bfa-b5b7-b09cd0f2f6c0"),sQuery(id+"F3.wireOp",EDGE,"8df1dcc8-d00a-4777-85fd-8af8e9830bd1"),sQuery(id+"F3.wireOp",EDGE,"26ce3762-0d1a-4b81-9a23-debcfc24da1c"),sQuery(id+"F3.wireOp",EDGE,"3e900f8f-3ffb-4e32-b536-61fea2f3e30a"),sQuery(id+"F3.wireOp",EDGE,"4a1b5445-5559-461f-b6f1-b4cd9b95ea10")])]});
            var Q4;
            Q4=makeQuery(id+"F1.opRevolve","SWEPT_BODY",BODY,{"disambiguationData":[OSD([sQuery(id+"F0.wireOp",EDGE,"E0"),sQuery(id+"F0.wireOp",EDGE,"E1")])]});
            var Q5;
            Q5=qCreatedBy(makeId("Origin.pointOp"),VERTEX);
            transform(context, id + "F5", {"entities" : qUnion([Q0, Q1, Q2, Q3, Q4]), "transformType" : TransformType.SCALE_UNIFORMLY, "scale" : 0.03, "scalePoint" : qUnion([Q5]), "makeCopy" : false});
        }
        {
            var Q0;
            Q0=qCreatedBy(makeId("Top.planeOp"),FACE);
            var sketch = newSketch(context, id + "F6", { "sketchPlane" : qUnion([Q0])});
            skLineSegment(sketch, "E544", {"start": v(0, 15) * mm, "end": v(0, -15) * mm});
            skArc(sketch, "E545", {"start": v(0, 15) * mm, "mid": v(-15, 0) * mm, "end": v(0, -15) * mm});
            skArc(sketch, "E546", {"start": v(0, 10.25) * mm, "mid": v(-10.25, 0) * mm, "end": v(0, -10.25) * mm});
            skArc(sketch, "E547", {"start": v(0, 7) * mm, "mid": v(-7, 0) * mm, "end": v(0, -7) * mm});
            skSolve(sketch);
        }
        {
            var Q0;
            {var subQ0=sQuery(id+"F6.wireOp",EDGE,"E545");Q0=makeQuery(id+"F6.imprint","IMPRINT",FACE,{"disambiguationData":[TD([[makeQuery(id+"F6.imprint","IMPRINT",EDGE,{"derivedFrom":subQ0}),1.0]])]});}
            var Q1;
            {var subQ0=sQuery(id+"F6.wireOp",EDGE,"E547");Q1=makeQuery(id+"F6.imprint","IMPRINT",FACE,{"disambiguationData":[TD([[makeQuery(id+"F6.imprint","IMPRINT",EDGE,{"derivedFrom":subQ0}),1.0]])]});}
            var Q2;
            Q2=sQuery(id+"F6.wireOp",EDGE,"E544");
            revolve(context, id + "F7", {"operationType" : NewBodyOperationType.REMOVE, "entities" : qUnion([Q0, Q1]), "axis" : qUnion([Q2]), "revolveType" : RevolveType.FULL});
        }
        {
            var Q0;
            Q0=makeQuery(id+"F1.opRevolve","SWEPT_BODY",BODY,{"disambiguationData":[OSD([sQuery(id+"F0.wireOp",EDGE,"E0"),sQuery(id+"F0.wireOp",EDGE,"E1")])]});
            var Q1;
            Q1=sQuery(id+"F0.wireOp",VERTEX,"E1.center");
            transform(context, id + "F8", {"entities" : qUnion([Q0]), "transformType" : TransformType.SCALE_UNIFORMLY, "scale" : 1.4, "scalePoint" : qUnion([Q1]), "makeCopy" : false});
        }
        {
            var Q0;
            Q0=qCreatedBy(makeId("Front.planeOp"),FACE);
            var sketch = newSketch(context, id + "F9", { "sketchPlane" : qUnion([Q0])});
            skCircle(sketch, "E548", {"center": v(0, -5.12) * mm, "radius": 2 * mm});
            skSolve(sketch);
        }
        {
            var Q0;
            Q0=qSketchRegion(id+"F9",true);
            extrude(context, id + "F10", {"entities" : qUnion([Q0]), "operationType" : NewBodyOperationType.REMOVE, "oppositeDirection" : true, "depth" : 25 * mm});
        }
        {
            var Q0;
            Q0=qCreatedBy(makeId("Top.planeOp"),FACE);
            var sketch = newSketch(context, id + "F11", { "sketchPlane" : qUnion([Q0])});
            skLineSegment(sketch, "E549", {"start": v(-21.3, 0) * mm, "end": v(28.76, 0) * mm});
            skArc(sketch, "E550", {"start": v(14.25, 0) * mm, "mid": v(0, -14.25) * mm, "end": v(-14.25, 0) * mm});
            skSolve(sketch);
        }
        {
            var Q0;
            Q0=sQuery(id+"F11.wireOp",EDGE,"E549");
            cPlane(context, id + "F12", {"entities" : qUnion([Q0]), "cplaneType" : CPlaneType.LINE_ANGLE, "offset" : 45 * mm, "angle" : 45 * degree, "width" : 150 * mm, "height" : 150 * mm});
        }
        {
            var Q0;
            Q0=qCreatedBy(id+"F12.planeOp",FACE);
            var sketch = newSketch(context, id + "F13", { "sketchPlane" : qUnion([Q0])});
            skText(sketch, "E551", { "text": "engineering", "fontName": "OpenSans-Italic.ttf"});
            const initialGuessF13  = {"E551": [-0.01268, -0.0025, 1, 0, 0.0035]};
            skSetInitialGuess(sketch, initialGuessF13);
            skSolve(sketch);
        }
        {
            var Q0;
            Q0=sQuery(id+"F11.wireOp",EDGE,"E550");
            var Q1;
            Q1=sQuery(id+"F11.wireOp",EDGE,"E549");
            revolve(context, id + "F14", {"bodyType" : ToolBodyType.SURFACE, "surfaceEntities" : qUnion([Q0]), "axis" : qUnion([Q1]), "revolveType" : RevolveType.FULL});
        }
        {
            var Q0;
            Q0 = qSketchRegion(id + "F13", true);
            var Q1;
            Q1=makeQuery(id+"F14.opRevolve","SWEPT_FACE",FACE,{"disambiguationData":[OSD([sQuery(id+"F11.wireOp",EDGE,"E550")])]});
            extrude(context, id + "F15", {"entities" : qUnion([Q0]), "operationType" : NewBodyOperationType.ADD, "endBound" : BoundingType.UP_TO_SURFACE, "depth" : 25 * mm, "endBoundEntityFace" : qUnion([Q1]), "offsetDistance" : 25 * mm});
        }
    });
